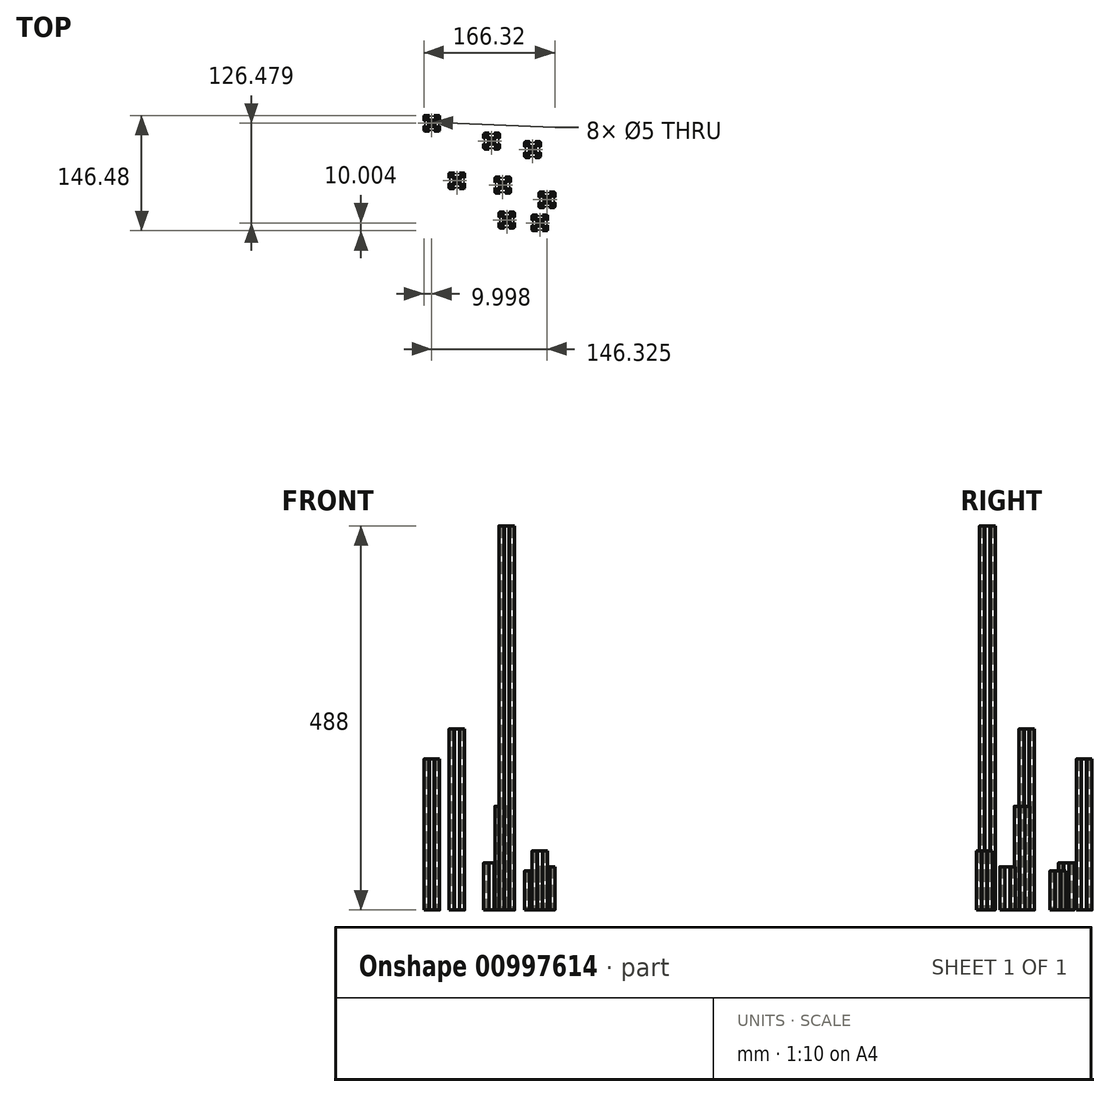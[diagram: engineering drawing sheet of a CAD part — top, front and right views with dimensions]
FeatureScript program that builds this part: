
annotation { "Feature Type Name" : "Feature", "Feature Type Description" : "" }
export const myFeature = defineFeature(function(context is Context, id is Id, definition is map)
    precondition{}
    {
        {
            var Q0;
            Q0=qCreatedBy(makeId("Top.planeOp"),FACE);
            var sketch = newSketch(context, id + "F0", { "sketchPlane" : qUnion([Q0])});
            skCircle(sketch, "E0", {"center": v(-239.3, 88.48) * mm, "radius": 2.5 * mm});
            skLineSegment(sketch, "E1.bottom", {"start": v(-230.8, 78.48) * mm, "end": v(-235.2, 78.48) * mm});
            skLineSegment(sketch, "E1.top", {"start": v(-230.8, 98.48) * mm, "end": v(-235.2, 98.48) * mm});
            skLineSegment(sketch, "E1.left", {"start": v(-229.3, 79.98) * mm, "end": v(-229.3, 84.88) * mm});
            skLineSegment(sketch, "E2.bottom", {"start": v(-237.3, 84.58) * mm, "end": v(-241.31, 84.58) * mm});
            skLineSegment(sketch, "E2.top", {"start": v(-237.3, 92.38) * mm, "end": v(-241.31, 92.38) * mm});
            skLineSegment(sketch, "E2.left", {"start": v(-235.4, 86.47) * mm, "end": v(-235.4, 90.5) * mm});
            skLineSegment(sketch, "E2.right", {"start": v(-243.2, 86.47) * mm, "end": v(-243.2, 90.5) * mm});
            skLineSegment(sketch, "E3.bottom", {"start": v(-230.8, 98.48) * mm, "end": v(-233.8, 98.48) * mm});
            skLineSegment(sketch, "E3.left", {"start": v(-229.3, 96.98) * mm, "end": v(-229.3, 93.98) * mm});
            skLineSegment(sketch, "E3.right", {"start": v(-233.8, 96.68) * mm, "end": v(-233.8, 95.04) * mm});
            skLineSegment(sketch, "E4", {"start": v(-234.82, 91.9) * mm, "end": v(-232.74, 93.98) * mm});
            skLineSegment(sketch, "E5.MirrorCS", {"start": v(-235.88, 92.97) * mm, "end": v(-233.8, 95.04) * mm});
            skLineSegment(sketch, "E6", {"start": v(-231.1, 93.98) * mm, "end": v(-231.1, 91.58) * mm});
            skLineSegment(sketch, "E7", {"start": v(-229.6, 92.08) * mm, "end": v(-229.3, 92.08) * mm});
            skLineSegment(sketch, "E8", {"start": v(-231.1, 91.58) * mm, "end": v(-229.8, 91.58) * mm});
            skLineSegment(sketch, "E9", {"start": v(-229.8, 91.88) * mm, "end": v(-229.8, 91.58) * mm});
            skPoint(sketch, "E10.visualSharp", {"position": v(-229.8, 92.08) * mm});
            skArc(sketch, "E10.filletArc", {"start": v(-229.6, 92.08) * mm, "mid": v(-229.74, 92.03) * mm, "end": v(-229.8, 91.88) * mm});
            skPoint(sketch, "E11.newPointA", {"position": v(-235.4, 91.32) * mm});
            skArc(sketch, "E11.filletArc", {"start": v(-234.82, 91.9) * mm, "mid": v(-235.25, 91.26) * mm, "end": v(-235.4, 90.5) * mm});
            skPoint(sketch, "E12.newPointA", {"position": v(-236.46, 92.38) * mm});
            skPoint(sketch, "E12.newPointB", {"position": v(-235.4, 92.38) * mm});
            skArc(sketch, "E12.filletArc", {"start": v(-237.3, 92.38) * mm, "mid": v(-236.53, 92.54) * mm, "end": v(-235.88, 92.97) * mm});
            skLineSegment(sketch, "E13.MirrorCS", {"start": v(-233.8, 96.68) * mm, "end": v(-236.2, 96.68) * mm});
            skLineSegment(sketch, "E14.MirrorCS", {"start": v(-236.2, 96.68) * mm, "end": v(-236.2, 97.98) * mm});
            skPoint(sketch, "E15.visualSharp", {"position": v(-229.3, 98.48) * mm});
            skArc(sketch, "E15.filletArc", {"start": v(-229.3, 96.98) * mm, "mid": v(-229.74, 98.04) * mm, "end": v(-230.8, 98.48) * mm});
            skLineSegment(sketch, "E16.trimOffspring", {"start": v(-231.1, 93.98) * mm, "end": v(-232.74, 93.98) * mm});
            skLineSegment(sketch, "E17.MirrorCS", {"start": v(-229.6, 84.88) * mm, "end": v(-229.3, 84.88) * mm});
            skArc(sketch, "E18.MirrorCS", {"start": v(-229.6, 84.88) * mm, "mid": v(-229.74, 84.94) * mm, "end": v(-229.8, 85.08) * mm});
            skLineSegment(sketch, "E19.MirrorCS", {"start": v(-229.8, 85.08) * mm, "end": v(-229.8, 85.38) * mm});
            skArc(sketch, "E20.MirrorCS", {"start": v(-234.82, 85.06) * mm, "mid": v(-235.25, 85.7) * mm, "end": v(-235.4, 86.47) * mm});
            skLineSegment(sketch, "E21.MirrorCS", {"start": v(-231.1, 82.98) * mm, "end": v(-232.74, 82.98) * mm});
            skLineSegment(sketch, "E22.MirrorCS", {"start": v(-231.1, 85.38) * mm, "end": v(-229.8, 85.38) * mm});
            skLineSegment(sketch, "E23.MirrorCS", {"start": v(-230.8, 78.48) * mm, "end": v(-233.8, 78.48) * mm});
            skPoint(sketch, "E24.MirrorP", {"position": v(-229.8, 84.88) * mm});
            skLineSegment(sketch, "E25.MirrorCS", {"start": v(-236.2, 80.28) * mm, "end": v(-236.2, 78.98) * mm});
            skLineSegment(sketch, "E26.MirrorCS", {"start": v(-233.8, 80.28) * mm, "end": v(-236.2, 80.28) * mm});
            skLineSegment(sketch, "E27.MirrorCS", {"start": v(-231.1, 82.98) * mm, "end": v(-231.1, 85.38) * mm});
            skLineSegment(sketch, "E28.MirrorCS", {"start": v(-229.3, 79.98) * mm, "end": v(-229.3, 82.98) * mm});
            skLineSegment(sketch, "E29.MirrorCS", {"start": v(-234.82, 85.06) * mm, "end": v(-232.74, 82.98) * mm});
            skPoint(sketch, "E30.MirrorP", {"position": v(-235.4, 85.64) * mm});
            skPoint(sketch, "E31.MirrorP", {"position": v(-229.3, 78.48) * mm});
            skPoint(sketch, "E32.MirrorP", {"position": v(-235.4, 84.58) * mm});
            skLineSegment(sketch, "E33.MirrorCS", {"start": v(-235.88, 84) * mm, "end": v(-233.8, 81.92) * mm});
            skPoint(sketch, "E34.MirrorP", {"position": v(-236.46, 84.58) * mm});
            skArc(sketch, "E35.MirrorCS", {"start": v(-229.3, 79.98) * mm, "mid": v(-229.74, 78.92) * mm, "end": v(-230.8, 78.48) * mm});
            skLineSegment(sketch, "E36.MirrorCS", {"start": v(-233.8, 80.28) * mm, "end": v(-233.8, 81.92) * mm});
            skArc(sketch, "E37.MirrorCS", {"start": v(-237.3, 84.58) * mm, "mid": v(-236.53, 84.43) * mm, "end": v(-235.88, 84) * mm});
            skLineSegment(sketch, "E38.trimOffspring", {"start": v(-229.3, 92.08) * mm, "end": v(-229.3, 96.98) * mm});
            skLineSegment(sketch, "E39.MirrorCS", {"start": v(-235.7, 98.18) * mm, "end": v(-235.7, 98.48) * mm});
            skArc(sketch, "E40.MirrorCS", {"start": v(-235.7, 98.18) * mm, "mid": v(-235.76, 98.04) * mm, "end": v(-235.9, 97.98) * mm});
            skLineSegment(sketch, "E41.MirrorCS", {"start": v(-235.9, 97.98) * mm, "end": v(-236.2, 97.98) * mm});
            skLineSegment(sketch, "E42", {"start": v(-235.2, 98.48) * mm, "end": v(-235.7, 98.48) * mm});
            skLineSegment(sketch, "E43.MirrorCS", {"start": v(-235.7, 78.78) * mm, "end": v(-235.7, 78.48) * mm});
            skLineSegment(sketch, "E44.MirrorCS", {"start": v(-235.9, 78.98) * mm, "end": v(-236.2, 78.98) * mm});
            skLineSegment(sketch, "E45.MirrorCS", {"start": v(-235.2, 78.48) * mm, "end": v(-235.7, 78.48) * mm});
            skArc(sketch, "E46.MirrorCS", {"start": v(-235.7, 78.78) * mm, "mid": v(-235.76, 78.93) * mm, "end": v(-235.9, 78.98) * mm});
            skArc(sketch, "E47.MirrorCS", {"start": v(-249, 84.88) * mm, "mid": v(-248.86, 84.94) * mm, "end": v(-248.8, 85.08) * mm});
            skLineSegment(sketch, "E48.MirrorCS", {"start": v(-249, 92.08) * mm, "end": v(-249.3, 92.08) * mm});
            skLineSegment(sketch, "E49.MirrorCS", {"start": v(-248.8, 85.08) * mm, "end": v(-248.8, 85.38) * mm});
            skArc(sketch, "E50.MirrorCS", {"start": v(-249, 92.08) * mm, "mid": v(-248.86, 92.03) * mm, "end": v(-248.8, 91.88) * mm});
            skLineSegment(sketch, "E51.MirrorCS", {"start": v(-248.8, 91.88) * mm, "end": v(-248.8, 91.58) * mm});
            skLineSegment(sketch, "E52.MirrorCS", {"start": v(-249, 84.88) * mm, "end": v(-249.3, 84.88) * mm});
            skLineSegment(sketch, "E53.MirrorCS", {"start": v(-243.4, 98.48) * mm, "end": v(-242.9, 98.48) * mm});
            skArc(sketch, "E54.MirrorCS", {"start": v(-249.3, 79.98) * mm, "mid": v(-248.86, 78.92) * mm, "end": v(-247.8, 78.48) * mm});
            skLineSegment(sketch, "E55.MirrorCS", {"start": v(-242.9, 98.18) * mm, "end": v(-242.9, 98.48) * mm});
            skArc(sketch, "E56.MirrorCS", {"start": v(-243.79, 91.9) * mm, "mid": v(-243.35, 91.26) * mm, "end": v(-243.2, 90.5) * mm});
            skLineSegment(sketch, "E57.MirrorCS", {"start": v(-242.7, 78.98) * mm, "end": v(-242.4, 78.98) * mm});
            skLineSegment(sketch, "E58.MirrorCS", {"start": v(-242.4, 96.68) * mm, "end": v(-242.4, 97.98) * mm});
            skLineSegment(sketch, "E59.MirrorCS", {"start": v(-241.31, 92.38) * mm, "end": v(-237.3, 92.38) * mm});
            skLineSegment(sketch, "E60.MirrorCS", {"start": v(-247.5, 85.38) * mm, "end": v(-248.8, 85.38) * mm});
            skLineSegment(sketch, "E61.MirrorCS", {"start": v(-247.5, 91.58) * mm, "end": v(-248.8, 91.58) * mm});
            skLineSegment(sketch, "E62.MirrorCS", {"start": v(-242.7, 97.98) * mm, "end": v(-242.4, 97.98) * mm});
            skArc(sketch, "E63.MirrorCS", {"start": v(-243.79, 85.06) * mm, "mid": v(-243.35, 85.7) * mm, "end": v(-243.2, 86.47) * mm});
            skArc(sketch, "E64.MirrorCS", {"start": v(-242.9, 78.78) * mm, "mid": v(-242.84, 78.93) * mm, "end": v(-242.7, 78.98) * mm});
            skArc(sketch, "E65.MirrorCS", {"start": v(-242.9, 98.18) * mm, "mid": v(-242.84, 98.04) * mm, "end": v(-242.7, 97.98) * mm});
            skLineSegment(sketch, "E66.MirrorCS", {"start": v(-242.9, 78.78) * mm, "end": v(-242.9, 78.48) * mm});
            skLineSegment(sketch, "E67.MirrorCS", {"start": v(-241.31, 84.58) * mm, "end": v(-237.3, 84.58) * mm});
            skLineSegment(sketch, "E68.MirrorCS", {"start": v(-243.4, 78.48) * mm, "end": v(-242.9, 78.48) * mm});
            skLineSegment(sketch, "E69.MirrorCS", {"start": v(-242.4, 80.28) * mm, "end": v(-242.4, 78.98) * mm});
            skArc(sketch, "E70.MirrorCS", {"start": v(-241.31, 92.38) * mm, "mid": v(-242.08, 92.54) * mm, "end": v(-242.73, 92.97) * mm});
            skPoint(sketch, "E71.MirrorP", {"position": v(-249.3, 78.48) * mm});
            skLineSegment(sketch, "E72.MirrorCS", {"start": v(-247.8, 78.48) * mm, "end": v(-243.4, 78.48) * mm});
            skPoint(sketch, "E73.MirrorP", {"position": v(-243.2, 84.58) * mm});
            skLineSegment(sketch, "E74.MirrorCS", {"start": v(-247.8, 98.48) * mm, "end": v(-243.4, 98.48) * mm});
            skArc(sketch, "E75.MirrorCS", {"start": v(-241.31, 84.58) * mm, "mid": v(-242.08, 84.43) * mm, "end": v(-242.73, 84) * mm});
            skArc(sketch, "E76.MirrorCS", {"start": v(-249.3, 96.98) * mm, "mid": v(-248.86, 98.04) * mm, "end": v(-247.8, 98.48) * mm});
            skPoint(sketch, "E77.MirrorP", {"position": v(-243.2, 85.64) * mm});
            skLineSegment(sketch, "E78.MirrorCS", {"start": v(-244.8, 96.68) * mm, "end": v(-244.8, 95.04) * mm});
            skLineSegment(sketch, "E79.MirrorCS", {"start": v(-242.73, 92.97) * mm, "end": v(-244.8, 95.04) * mm});
            skPoint(sketch, "E80.MirrorP", {"position": v(-243.2, 91.32) * mm});
            skLineSegment(sketch, "E81.MirrorCS", {"start": v(-247.5, 82.98) * mm, "end": v(-247.5, 85.38) * mm});
            skLineSegment(sketch, "E82.MirrorCS", {"start": v(-243.79, 85.06) * mm, "end": v(-245.86, 82.98) * mm});
            skLineSegment(sketch, "E83.MirrorCS", {"start": v(-244.8, 80.28) * mm, "end": v(-242.4, 80.28) * mm});
            skLineSegment(sketch, "E84.MirrorCS", {"start": v(-247.5, 82.98) * mm, "end": v(-245.86, 82.98) * mm});
            skLineSegment(sketch, "E85.MirrorCS", {"start": v(-249.3, 79.98) * mm, "end": v(-249.3, 82.98) * mm});
            skLineSegment(sketch, "E86.MirrorCS", {"start": v(-247.8, 98.48) * mm, "end": v(-244.8, 98.48) * mm});
            skLineSegment(sketch, "E87.MirrorCS", {"start": v(-249.3, 92.08) * mm, "end": v(-249.3, 96.98) * mm});
            skLineSegment(sketch, "E88.MirrorCS", {"start": v(-244.8, 96.68) * mm, "end": v(-242.4, 96.68) * mm});
            skLineSegment(sketch, "E89.MirrorCS", {"start": v(-242.73, 84) * mm, "end": v(-244.8, 81.92) * mm});
            skPoint(sketch, "E90.MirrorP", {"position": v(-242.14, 84.58) * mm});
            skLineSegment(sketch, "E91.MirrorCS", {"start": v(-247.5, 93.98) * mm, "end": v(-247.5, 91.58) * mm});
            skLineSegment(sketch, "E92.MirrorCS", {"start": v(-249.3, 96.98) * mm, "end": v(-249.3, 93.98) * mm});
            skPoint(sketch, "E93.MirrorP", {"position": v(-248.8, 84.88) * mm});
            skPoint(sketch, "E94.MirrorP", {"position": v(-249.3, 98.48) * mm});
            skPoint(sketch, "E95.MirrorP", {"position": v(-248.8, 92.08) * mm});
            skLineSegment(sketch, "E96.MirrorCS", {"start": v(-243.79, 91.9) * mm, "end": v(-245.86, 93.98) * mm});
            skLineSegment(sketch, "E97.MirrorCS", {"start": v(-247.5, 93.98) * mm, "end": v(-245.86, 93.98) * mm});
            skLineSegment(sketch, "E98.MirrorCS", {"start": v(-249.3, 79.98) * mm, "end": v(-249.3, 84.88) * mm});
            skLineSegment(sketch, "E99.MirrorCS", {"start": v(-247.8, 78.48) * mm, "end": v(-244.8, 78.48) * mm});
            skPoint(sketch, "E100.MirrorP", {"position": v(-243.2, 92.38) * mm});
            skPoint(sketch, "E101.MirrorP", {"position": v(-242.14, 92.38) * mm});
            skLineSegment(sketch, "E102.MirrorCS", {"start": v(-244.8, 80.28) * mm, "end": v(-244.8, 81.92) * mm});
            skSolve(sketch);
        }
        {
            var Q0;
            Q0=makeQuery(id+"F0.imprint","IMPRINT",FACE,{"disambiguationData":[TD([[makeQuery(id+"F0.imprint","IMPRINT",EDGE,{"derivedFrom":sQuery(id+"F0.wireOp",EDGE,"E1.bottom")}),-1.0]])]});
            extrude(context, id + "F1", {"entities" : qUnion([Q0]), "depth" : 192 * mm, "offsetDistance" : 25 * mm});
        }
        {
            var Q0;
            Q0=qCreatedBy(makeId("Top.planeOp"),FACE);
            var sketch = newSketch(context, id + "F2", { "sketchPlane" : qUnion([Q0])});
            skCircle(sketch, "E103", {"center": v(-207.4, 15.55) * mm, "radius": 2.5 * mm});
            skLineSegment(sketch, "E104.bottom", {"start": v(-198.9, 5.55) * mm, "end": v(-203.3, 5.55) * mm});
            skLineSegment(sketch, "E104.top", {"start": v(-198.9, 25.55) * mm, "end": v(-203.3, 25.55) * mm});
            skLineSegment(sketch, "E104.left", {"start": v(-197.4, 7.05) * mm, "end": v(-197.4, 11.95) * mm});
            skLineSegment(sketch, "E105.bottom", {"start": v(-205.4, 11.65) * mm, "end": v(-209.42, 11.65) * mm});
            skLineSegment(sketch, "E105.top", {"start": v(-205.4, 19.45) * mm, "end": v(-209.42, 19.45) * mm});
            skLineSegment(sketch, "E105.left", {"start": v(-203.5, 13.54) * mm, "end": v(-203.5, 17.56) * mm});
            skLineSegment(sketch, "E105.right", {"start": v(-211.3, 13.54) * mm, "end": v(-211.3, 17.56) * mm});
            skLineSegment(sketch, "E106.bottom", {"start": v(-198.9, 25.55) * mm, "end": v(-201.9, 25.55) * mm});
            skLineSegment(sketch, "E106.left", {"start": v(-197.4, 24.05) * mm, "end": v(-197.4, 21.05) * mm});
            skLineSegment(sketch, "E106.right", {"start": v(-201.9, 23.75) * mm, "end": v(-201.9, 22.1) * mm});
            skLineSegment(sketch, "E107", {"start": v(-202.92, 18.97) * mm, "end": v(-200.84, 21.05) * mm});
            skLineSegment(sketch, "E108.MirrorCS", {"start": v(-203.98, 20.04) * mm, "end": v(-201.9, 22.1) * mm});
            skLineSegment(sketch, "E109", {"start": v(-199.2, 21.05) * mm, "end": v(-199.2, 18.65) * mm});
            skLineSegment(sketch, "E110", {"start": v(-197.7, 19.15) * mm, "end": v(-197.4, 19.15) * mm});
            skLineSegment(sketch, "E111", {"start": v(-199.2, 18.65) * mm, "end": v(-197.9, 18.65) * mm});
            skLineSegment(sketch, "E112", {"start": v(-197.9, 18.95) * mm, "end": v(-197.9, 18.65) * mm});
            skPoint(sketch, "E113.visualSharp", {"position": v(-197.9, 19.15) * mm});
            skArc(sketch, "E113.filletArc", {"start": v(-197.7, 19.15) * mm, "mid": v(-197.85, 19.1) * mm, "end": v(-197.9, 18.95) * mm});
            skPoint(sketch, "E114.newPointA", {"position": v(-203.5, 18.39) * mm});
            skArc(sketch, "E114.filletArc", {"start": v(-202.92, 18.97) * mm, "mid": v(-203.35, 18.33) * mm, "end": v(-203.5, 17.56) * mm});
            skPoint(sketch, "E115.newPointA", {"position": v(-204.57, 19.45) * mm});
            skPoint(sketch, "E115.newPointB", {"position": v(-203.5, 19.45) * mm});
            skArc(sketch, "E115.filletArc", {"start": v(-205.4, 19.45) * mm, "mid": v(-204.63, 19.6) * mm, "end": v(-203.98, 20.04) * mm});
            skLineSegment(sketch, "E116.MirrorCS", {"start": v(-201.9, 23.75) * mm, "end": v(-204.3, 23.75) * mm});
            skLineSegment(sketch, "E117.MirrorCS", {"start": v(-204.3, 23.75) * mm, "end": v(-204.3, 25.05) * mm});
            skPoint(sketch, "E118.visualSharp", {"position": v(-197.4, 25.55) * mm});
            skArc(sketch, "E118.filletArc", {"start": v(-197.4, 24.05) * mm, "mid": v(-197.84, 25.1) * mm, "end": v(-198.9, 25.55) * mm});
            skLineSegment(sketch, "E119.trimOffspring", {"start": v(-199.2, 21.05) * mm, "end": v(-200.84, 21.05) * mm});
            skLineSegment(sketch, "E120.MirrorCS", {"start": v(-197.7, 11.95) * mm, "end": v(-197.4, 11.95) * mm});
            skArc(sketch, "E121.MirrorCS", {"start": v(-197.7, 11.95) * mm, "mid": v(-197.85, 12) * mm, "end": v(-197.9, 12.15) * mm});
            skLineSegment(sketch, "E122.MirrorCS", {"start": v(-197.9, 12.15) * mm, "end": v(-197.9, 12.45) * mm});
            skArc(sketch, "E123.MirrorCS", {"start": v(-202.92, 12.12) * mm, "mid": v(-203.35, 12.77) * mm, "end": v(-203.5, 13.54) * mm});
            skLineSegment(sketch, "E124.MirrorCS", {"start": v(-199.2, 10.05) * mm, "end": v(-200.84, 10.05) * mm});
            skLineSegment(sketch, "E125.MirrorCS", {"start": v(-199.2, 12.45) * mm, "end": v(-197.9, 12.45) * mm});
            skLineSegment(sketch, "E126.MirrorCS", {"start": v(-198.9, 5.55) * mm, "end": v(-201.9, 5.55) * mm});
            skPoint(sketch, "E127.MirrorP", {"position": v(-197.9, 11.95) * mm});
            skLineSegment(sketch, "E128.MirrorCS", {"start": v(-204.3, 7.35) * mm, "end": v(-204.3, 6.05) * mm});
            skLineSegment(sketch, "E129.MirrorCS", {"start": v(-201.9, 7.35) * mm, "end": v(-204.3, 7.35) * mm});
            skLineSegment(sketch, "E130.MirrorCS", {"start": v(-199.2, 10.05) * mm, "end": v(-199.2, 12.45) * mm});
            skLineSegment(sketch, "E131.MirrorCS", {"start": v(-197.4, 7.05) * mm, "end": v(-197.4, 10.05) * mm});
            skLineSegment(sketch, "E132.MirrorCS", {"start": v(-202.92, 12.12) * mm, "end": v(-200.84, 10.05) * mm});
            skPoint(sketch, "E133.MirrorP", {"position": v(-203.5, 12.7) * mm});
            skPoint(sketch, "E134.MirrorP", {"position": v(-197.4, 5.55) * mm});
            skPoint(sketch, "E135.MirrorP", {"position": v(-203.5, 11.65) * mm});
            skLineSegment(sketch, "E136.MirrorCS", {"start": v(-203.98, 11.06) * mm, "end": v(-201.9, 8.99) * mm});
            skPoint(sketch, "E137.MirrorP", {"position": v(-204.57, 11.65) * mm});
            skArc(sketch, "E138.MirrorCS", {"start": v(-197.4, 7.05) * mm, "mid": v(-197.84, 5.99) * mm, "end": v(-198.9, 5.55) * mm});
            skLineSegment(sketch, "E139.MirrorCS", {"start": v(-201.9, 7.35) * mm, "end": v(-201.9, 8.99) * mm});
            skArc(sketch, "E140.MirrorCS", {"start": v(-205.4, 11.65) * mm, "mid": v(-204.63, 11.5) * mm, "end": v(-203.98, 11.06) * mm});
            skLineSegment(sketch, "E141.trimOffspring", {"start": v(-197.4, 19.15) * mm, "end": v(-197.4, 24.05) * mm});
            skLineSegment(sketch, "E142.MirrorCS", {"start": v(-203.8, 25.25) * mm, "end": v(-203.8, 25.55) * mm});
            skArc(sketch, "E143.MirrorCS", {"start": v(-203.8, 25.25) * mm, "mid": v(-203.86, 25.1) * mm, "end": v(-204, 25.05) * mm});
            skLineSegment(sketch, "E144.MirrorCS", {"start": v(-204, 25.05) * mm, "end": v(-204.3, 25.05) * mm});
            skLineSegment(sketch, "E145", {"start": v(-203.3, 25.55) * mm, "end": v(-203.8, 25.55) * mm});
            skLineSegment(sketch, "E146.MirrorCS", {"start": v(-203.8, 5.85) * mm, "end": v(-203.8, 5.55) * mm});
            skLineSegment(sketch, "E147.MirrorCS", {"start": v(-204, 6.05) * mm, "end": v(-204.3, 6.05) * mm});
            skLineSegment(sketch, "E148.MirrorCS", {"start": v(-203.3, 5.55) * mm, "end": v(-203.8, 5.55) * mm});
            skArc(sketch, "E149.MirrorCS", {"start": v(-203.8, 5.85) * mm, "mid": v(-203.86, 6) * mm, "end": v(-204, 6.05) * mm});
            skArc(sketch, "E150.MirrorCS", {"start": v(-217.1, 11.95) * mm, "mid": v(-216.96, 12) * mm, "end": v(-216.9, 12.15) * mm});
            skLineSegment(sketch, "E151.MirrorCS", {"start": v(-217.1, 19.15) * mm, "end": v(-217.4, 19.15) * mm});
            skLineSegment(sketch, "E152.MirrorCS", {"start": v(-216.9, 12.15) * mm, "end": v(-216.9, 12.45) * mm});
            skArc(sketch, "E153.MirrorCS", {"start": v(-217.1, 19.15) * mm, "mid": v(-216.96, 19.1) * mm, "end": v(-216.9, 18.95) * mm});
            skLineSegment(sketch, "E154.MirrorCS", {"start": v(-216.9, 18.95) * mm, "end": v(-216.9, 18.65) * mm});
            skLineSegment(sketch, "E155.MirrorCS", {"start": v(-217.1, 11.95) * mm, "end": v(-217.4, 11.95) * mm});
            skLineSegment(sketch, "E156.MirrorCS", {"start": v(-211.5, 25.55) * mm, "end": v(-211, 25.55) * mm});
            skArc(sketch, "E157.MirrorCS", {"start": v(-217.4, 7.05) * mm, "mid": v(-216.97, 5.99) * mm, "end": v(-215.9, 5.55) * mm});
            skLineSegment(sketch, "E158.MirrorCS", {"start": v(-211, 25.25) * mm, "end": v(-211, 25.55) * mm});
            skArc(sketch, "E159.MirrorCS", {"start": v(-211.9, 18.97) * mm, "mid": v(-211.46, 18.33) * mm, "end": v(-211.3, 17.56) * mm});
            skLineSegment(sketch, "E160.MirrorCS", {"start": v(-210.8, 6.05) * mm, "end": v(-210.5, 6.05) * mm});
            skLineSegment(sketch, "E161.MirrorCS", {"start": v(-210.5, 23.75) * mm, "end": v(-210.5, 25.05) * mm});
            skLineSegment(sketch, "E162.MirrorCS", {"start": v(-209.42, 19.45) * mm, "end": v(-205.4, 19.45) * mm});
            skLineSegment(sketch, "E163.MirrorCS", {"start": v(-215.6, 12.45) * mm, "end": v(-216.9, 12.45) * mm});
            skLineSegment(sketch, "E164.MirrorCS", {"start": v(-215.6, 18.65) * mm, "end": v(-216.9, 18.65) * mm});
            skLineSegment(sketch, "E165.MirrorCS", {"start": v(-210.8, 25.05) * mm, "end": v(-210.5, 25.05) * mm});
            skArc(sketch, "E166.MirrorCS", {"start": v(-211.9, 12.12) * mm, "mid": v(-211.46, 12.77) * mm, "end": v(-211.3, 13.54) * mm});
            skArc(sketch, "E167.MirrorCS", {"start": v(-211, 5.85) * mm, "mid": v(-210.95, 6) * mm, "end": v(-210.8, 6.05) * mm});
            skArc(sketch, "E168.MirrorCS", {"start": v(-211, 25.25) * mm, "mid": v(-210.95, 25.1) * mm, "end": v(-210.8, 25.05) * mm});
            skLineSegment(sketch, "E169.MirrorCS", {"start": v(-211, 5.85) * mm, "end": v(-211, 5.55) * mm});
            skLineSegment(sketch, "E170.MirrorCS", {"start": v(-209.42, 11.65) * mm, "end": v(-205.4, 11.65) * mm});
            skLineSegment(sketch, "E171.MirrorCS", {"start": v(-211.5, 5.55) * mm, "end": v(-211, 5.55) * mm});
            skLineSegment(sketch, "E172.MirrorCS", {"start": v(-210.5, 7.35) * mm, "end": v(-210.5, 6.05) * mm});
            skArc(sketch, "E173.MirrorCS", {"start": v(-209.42, 19.45) * mm, "mid": v(-210.18, 19.6) * mm, "end": v(-210.83, 20.04) * mm});
            skPoint(sketch, "E174.MirrorP", {"position": v(-217.4, 5.55) * mm});
            skLineSegment(sketch, "E175.MirrorCS", {"start": v(-215.9, 5.55) * mm, "end": v(-211.5, 5.55) * mm});
            skPoint(sketch, "E176.MirrorP", {"position": v(-211.3, 11.65) * mm});
            skLineSegment(sketch, "E177.MirrorCS", {"start": v(-215.9, 25.55) * mm, "end": v(-211.5, 25.55) * mm});
            skArc(sketch, "E178.MirrorCS", {"start": v(-209.42, 11.65) * mm, "mid": v(-210.18, 11.5) * mm, "end": v(-210.83, 11.06) * mm});
            skArc(sketch, "E179.MirrorCS", {"start": v(-217.4, 24.05) * mm, "mid": v(-216.97, 25.1) * mm, "end": v(-215.9, 25.55) * mm});
            skPoint(sketch, "E180.MirrorP", {"position": v(-211.3, 12.7) * mm});
            skLineSegment(sketch, "E181.MirrorCS", {"start": v(-212.9, 23.75) * mm, "end": v(-212.9, 22.1) * mm});
            skLineSegment(sketch, "E182.MirrorCS", {"start": v(-210.83, 20.04) * mm, "end": v(-212.9, 22.1) * mm});
            skPoint(sketch, "E183.MirrorP", {"position": v(-211.3, 18.39) * mm});
            skLineSegment(sketch, "E184.MirrorCS", {"start": v(-215.6, 10.05) * mm, "end": v(-215.6, 12.45) * mm});
            skLineSegment(sketch, "E185.MirrorCS", {"start": v(-211.9, 12.12) * mm, "end": v(-213.97, 10.05) * mm});
            skLineSegment(sketch, "E186.MirrorCS", {"start": v(-212.9, 7.35) * mm, "end": v(-210.5, 7.35) * mm});
            skLineSegment(sketch, "E187.MirrorCS", {"start": v(-215.6, 10.05) * mm, "end": v(-213.97, 10.05) * mm});
            skLineSegment(sketch, "E188.MirrorCS", {"start": v(-217.4, 7.05) * mm, "end": v(-217.4, 10.05) * mm});
            skLineSegment(sketch, "E189.MirrorCS", {"start": v(-215.9, 25.55) * mm, "end": v(-212.9, 25.55) * mm});
            skLineSegment(sketch, "E190.MirrorCS", {"start": v(-217.4, 19.15) * mm, "end": v(-217.4, 24.05) * mm});
            skLineSegment(sketch, "E191.MirrorCS", {"start": v(-212.9, 23.75) * mm, "end": v(-210.5, 23.75) * mm});
            skLineSegment(sketch, "E192.MirrorCS", {"start": v(-210.83, 11.06) * mm, "end": v(-212.9, 8.99) * mm});
            skPoint(sketch, "E193.MirrorP", {"position": v(-210.24, 11.65) * mm});
            skLineSegment(sketch, "E194.MirrorCS", {"start": v(-215.6, 21.05) * mm, "end": v(-215.6, 18.65) * mm});
            skLineSegment(sketch, "E195.MirrorCS", {"start": v(-217.4, 24.05) * mm, "end": v(-217.4, 21.05) * mm});
            skPoint(sketch, "E196.MirrorP", {"position": v(-216.9, 11.95) * mm});
            skPoint(sketch, "E197.MirrorP", {"position": v(-217.4, 25.55) * mm});
            skPoint(sketch, "E198.MirrorP", {"position": v(-216.9, 19.15) * mm});
            skLineSegment(sketch, "E199.MirrorCS", {"start": v(-211.9, 18.97) * mm, "end": v(-213.97, 21.05) * mm});
            skLineSegment(sketch, "E200.MirrorCS", {"start": v(-215.6, 21.05) * mm, "end": v(-213.97, 21.05) * mm});
            skLineSegment(sketch, "E201.MirrorCS", {"start": v(-217.4, 7.05) * mm, "end": v(-217.4, 11.95) * mm});
            skLineSegment(sketch, "E202.MirrorCS", {"start": v(-215.9, 5.55) * mm, "end": v(-212.9, 5.55) * mm});
            skPoint(sketch, "E203.MirrorP", {"position": v(-211.3, 19.45) * mm});
            skPoint(sketch, "E204.MirrorP", {"position": v(-210.24, 19.45) * mm});
            skLineSegment(sketch, "E205.MirrorCS", {"start": v(-212.9, 7.35) * mm, "end": v(-212.9, 8.99) * mm});
            skSolve(sketch);
        }
        {
            var Q0;
            Q0=makeQuery(id+"F2.imprint","IMPRINT",FACE,{"disambiguationData":[TD([[makeQuery(id+"F2.imprint","IMPRINT",EDGE,{"derivedFrom":sQuery(id+"F2.wireOp",EDGE,"E104.bottom")}),-1.0]])]});
            extrude(context, id + "F3", {"entities" : qUnion([Q0]), "depth" : 230 * mm, "offsetDistance" : 25 * mm});
        }
        {
            var Q0;
            Q0=qCreatedBy(makeId("Top.planeOp"),FACE);
            var sketch = newSketch(context, id + "F4", { "sketchPlane" : qUnion([Q0])});
            skCircle(sketch, "E206", {"center": v(-163.25, 65.95) * mm, "radius": 2.5 * mm});
            skLineSegment(sketch, "E207.bottom", {"start": v(-154.75, 55.95) * mm, "end": v(-159.15, 55.95) * mm});
            skLineSegment(sketch, "E207.top", {"start": v(-154.75, 75.95) * mm, "end": v(-159.15, 75.95) * mm});
            skLineSegment(sketch, "E207.left", {"start": v(-153.25, 57.45) * mm, "end": v(-153.25, 62.35) * mm});
            skLineSegment(sketch, "E208.bottom", {"start": v(-161.24, 62.05) * mm, "end": v(-165.26, 62.05) * mm});
            skLineSegment(sketch, "E208.top", {"start": v(-161.24, 69.85) * mm, "end": v(-165.26, 69.85) * mm});
            skLineSegment(sketch, "E208.left", {"start": v(-159.35, 63.94) * mm, "end": v(-159.35, 67.96) * mm});
            skLineSegment(sketch, "E208.right", {"start": v(-167.15, 63.94) * mm, "end": v(-167.15, 67.96) * mm});
            skLineSegment(sketch, "E209.bottom", {"start": v(-154.75, 75.95) * mm, "end": v(-157.75, 75.95) * mm});
            skLineSegment(sketch, "E209.left", {"start": v(-153.25, 74.45) * mm, "end": v(-153.25, 71.45) * mm});
            skLineSegment(sketch, "E209.right", {"start": v(-157.75, 74.15) * mm, "end": v(-157.75, 72.51) * mm});
            skLineSegment(sketch, "E210", {"start": v(-158.76, 69.38) * mm, "end": v(-156.69, 71.45) * mm});
            skLineSegment(sketch, "E211.MirrorCS", {"start": v(-159.82, 70.44) * mm, "end": v(-157.75, 72.51) * mm});
            skLineSegment(sketch, "E212", {"start": v(-155.05, 71.45) * mm, "end": v(-155.05, 69.05) * mm});
            skLineSegment(sketch, "E213", {"start": v(-153.55, 69.55) * mm, "end": v(-153.25, 69.55) * mm});
            skLineSegment(sketch, "E214", {"start": v(-155.05, 69.05) * mm, "end": v(-153.75, 69.05) * mm});
            skLineSegment(sketch, "E215", {"start": v(-153.75, 69.35) * mm, "end": v(-153.75, 69.05) * mm});
            skPoint(sketch, "E216.visualSharp", {"position": v(-153.75, 69.55) * mm});
            skArc(sketch, "E216.filletArc", {"start": v(-153.55, 69.55) * mm, "mid": v(-153.7, 69.5) * mm, "end": v(-153.75, 69.35) * mm});
            skPoint(sketch, "E217.newPointA", {"position": v(-159.35, 68.8) * mm});
            skArc(sketch, "E217.filletArc", {"start": v(-158.76, 69.38) * mm, "mid": v(-159.2, 68.73) * mm, "end": v(-159.35, 67.96) * mm});
            skPoint(sketch, "E218.newPointA", {"position": v(-160.41, 69.85) * mm});
            skPoint(sketch, "E218.newPointB", {"position": v(-159.35, 69.85) * mm});
            skArc(sketch, "E218.filletArc", {"start": v(-161.24, 69.85) * mm, "mid": v(-160.47, 70) * mm, "end": v(-159.82, 70.44) * mm});
            skLineSegment(sketch, "E219.MirrorCS", {"start": v(-157.75, 74.15) * mm, "end": v(-160.15, 74.15) * mm});
            skLineSegment(sketch, "E220.MirrorCS", {"start": v(-160.15, 74.15) * mm, "end": v(-160.15, 75.45) * mm});
            skPoint(sketch, "E221.visualSharp", {"position": v(-153.25, 75.95) * mm});
            skArc(sketch, "E221.filletArc", {"start": v(-153.25, 74.45) * mm, "mid": v(-153.69, 75.51) * mm, "end": v(-154.75, 75.95) * mm});
            skLineSegment(sketch, "E222.trimOffspring", {"start": v(-155.05, 71.45) * mm, "end": v(-156.69, 71.45) * mm});
            skLineSegment(sketch, "E223.MirrorCS", {"start": v(-153.55, 62.35) * mm, "end": v(-153.25, 62.35) * mm});
            skArc(sketch, "E224.MirrorCS", {"start": v(-153.55, 62.35) * mm, "mid": v(-153.7, 62.4) * mm, "end": v(-153.75, 62.55) * mm});
            skLineSegment(sketch, "E225.MirrorCS", {"start": v(-153.75, 62.55) * mm, "end": v(-153.75, 62.85) * mm});
            skArc(sketch, "E226.MirrorCS", {"start": v(-158.76, 62.53) * mm, "mid": v(-159.2, 63.17) * mm, "end": v(-159.35, 63.94) * mm});
            skLineSegment(sketch, "E227.MirrorCS", {"start": v(-155.05, 60.45) * mm, "end": v(-156.69, 60.45) * mm});
            skLineSegment(sketch, "E228.MirrorCS", {"start": v(-155.05, 62.85) * mm, "end": v(-153.75, 62.85) * mm});
            skLineSegment(sketch, "E229.MirrorCS", {"start": v(-154.75, 55.95) * mm, "end": v(-157.75, 55.95) * mm});
            skPoint(sketch, "E230.MirrorP", {"position": v(-153.75, 62.35) * mm});
            skLineSegment(sketch, "E231.MirrorCS", {"start": v(-160.15, 57.75) * mm, "end": v(-160.15, 56.45) * mm});
            skLineSegment(sketch, "E232.MirrorCS", {"start": v(-157.75, 57.75) * mm, "end": v(-160.15, 57.75) * mm});
            skLineSegment(sketch, "E233.MirrorCS", {"start": v(-155.05, 60.45) * mm, "end": v(-155.05, 62.85) * mm});
            skLineSegment(sketch, "E234.MirrorCS", {"start": v(-153.25, 57.45) * mm, "end": v(-153.25, 60.45) * mm});
            skLineSegment(sketch, "E235.MirrorCS", {"start": v(-158.76, 62.53) * mm, "end": v(-156.69, 60.45) * mm});
            skPoint(sketch, "E236.MirrorP", {"position": v(-159.35, 63.11) * mm});
            skPoint(sketch, "E237.MirrorP", {"position": v(-153.25, 55.95) * mm});
            skPoint(sketch, "E238.MirrorP", {"position": v(-159.35, 62.05) * mm});
            skLineSegment(sketch, "E239.MirrorCS", {"start": v(-159.82, 61.47) * mm, "end": v(-157.75, 59.4) * mm});
            skPoint(sketch, "E240.MirrorP", {"position": v(-160.41, 62.05) * mm});
            skArc(sketch, "E241.MirrorCS", {"start": v(-153.25, 57.45) * mm, "mid": v(-153.69, 56.4) * mm, "end": v(-154.75, 55.95) * mm});
            skLineSegment(sketch, "E242.MirrorCS", {"start": v(-157.75, 57.75) * mm, "end": v(-157.75, 59.4) * mm});
            skArc(sketch, "E243.MirrorCS", {"start": v(-161.24, 62.05) * mm, "mid": v(-160.47, 61.9) * mm, "end": v(-159.82, 61.47) * mm});
            skLineSegment(sketch, "E244.trimOffspring", {"start": v(-153.25, 69.55) * mm, "end": v(-153.25, 74.45) * mm});
            skLineSegment(sketch, "E245.MirrorCS", {"start": v(-159.65, 75.65) * mm, "end": v(-159.65, 75.95) * mm});
            skArc(sketch, "E246.MirrorCS", {"start": v(-159.65, 75.65) * mm, "mid": v(-159.7, 75.5) * mm, "end": v(-159.85, 75.45) * mm});
            skLineSegment(sketch, "E247.MirrorCS", {"start": v(-159.85, 75.45) * mm, "end": v(-160.15, 75.45) * mm});
            skLineSegment(sketch, "E248", {"start": v(-159.15, 75.95) * mm, "end": v(-159.65, 75.95) * mm});
            skLineSegment(sketch, "E249.MirrorCS", {"start": v(-159.65, 56.25) * mm, "end": v(-159.65, 55.95) * mm});
            skLineSegment(sketch, "E250.MirrorCS", {"start": v(-159.85, 56.45) * mm, "end": v(-160.15, 56.45) * mm});
            skLineSegment(sketch, "E251.MirrorCS", {"start": v(-159.15, 55.95) * mm, "end": v(-159.65, 55.95) * mm});
            skArc(sketch, "E252.MirrorCS", {"start": v(-159.65, 56.25) * mm, "mid": v(-159.7, 56.4) * mm, "end": v(-159.85, 56.45) * mm});
            skArc(sketch, "E253.MirrorCS", {"start": v(-172.95, 62.35) * mm, "mid": v(-172.8, 62.4) * mm, "end": v(-172.75, 62.55) * mm});
            skLineSegment(sketch, "E254.MirrorCS", {"start": v(-172.95, 69.55) * mm, "end": v(-173.25, 69.55) * mm});
            skLineSegment(sketch, "E255.MirrorCS", {"start": v(-172.75, 62.55) * mm, "end": v(-172.75, 62.85) * mm});
            skArc(sketch, "E256.MirrorCS", {"start": v(-172.95, 69.55) * mm, "mid": v(-172.8, 69.5) * mm, "end": v(-172.75, 69.35) * mm});
            skLineSegment(sketch, "E257.MirrorCS", {"start": v(-172.75, 69.35) * mm, "end": v(-172.75, 69.05) * mm});
            skLineSegment(sketch, "E258.MirrorCS", {"start": v(-172.95, 62.35) * mm, "end": v(-173.25, 62.35) * mm});
            skLineSegment(sketch, "E259.MirrorCS", {"start": v(-167.35, 75.95) * mm, "end": v(-166.85, 75.95) * mm});
            skArc(sketch, "E260.MirrorCS", {"start": v(-173.25, 57.45) * mm, "mid": v(-172.81, 56.4) * mm, "end": v(-171.75, 55.95) * mm});
            skLineSegment(sketch, "E261.MirrorCS", {"start": v(-166.85, 75.65) * mm, "end": v(-166.85, 75.95) * mm});
            skArc(sketch, "E262.MirrorCS", {"start": v(-167.74, 69.38) * mm, "mid": v(-167.3, 68.73) * mm, "end": v(-167.15, 67.96) * mm});
            skLineSegment(sketch, "E263.MirrorCS", {"start": v(-166.65, 56.45) * mm, "end": v(-166.35, 56.45) * mm});
            skLineSegment(sketch, "E264.MirrorCS", {"start": v(-166.35, 74.15) * mm, "end": v(-166.35, 75.45) * mm});
            skLineSegment(sketch, "E265.MirrorCS", {"start": v(-165.26, 69.85) * mm, "end": v(-161.24, 69.85) * mm});
            skLineSegment(sketch, "E266.MirrorCS", {"start": v(-171.45, 62.85) * mm, "end": v(-172.75, 62.85) * mm});
            skLineSegment(sketch, "E267.MirrorCS", {"start": v(-171.45, 69.05) * mm, "end": v(-172.75, 69.05) * mm});
            skLineSegment(sketch, "E268.MirrorCS", {"start": v(-166.65, 75.45) * mm, "end": v(-166.35, 75.45) * mm});
            skArc(sketch, "E269.MirrorCS", {"start": v(-167.74, 62.53) * mm, "mid": v(-167.3, 63.17) * mm, "end": v(-167.15, 63.94) * mm});
            skArc(sketch, "E270.MirrorCS", {"start": v(-166.85, 56.25) * mm, "mid": v(-166.8, 56.4) * mm, "end": v(-166.65, 56.45) * mm});
            skArc(sketch, "E271.MirrorCS", {"start": v(-166.85, 75.65) * mm, "mid": v(-166.8, 75.5) * mm, "end": v(-166.65, 75.45) * mm});
            skLineSegment(sketch, "E272.MirrorCS", {"start": v(-166.85, 56.25) * mm, "end": v(-166.85, 55.95) * mm});
            skLineSegment(sketch, "E273.MirrorCS", {"start": v(-165.26, 62.05) * mm, "end": v(-161.24, 62.05) * mm});
            skLineSegment(sketch, "E274.MirrorCS", {"start": v(-167.35, 55.95) * mm, "end": v(-166.85, 55.95) * mm});
            skLineSegment(sketch, "E275.MirrorCS", {"start": v(-166.35, 57.75) * mm, "end": v(-166.35, 56.45) * mm});
            skArc(sketch, "E276.MirrorCS", {"start": v(-165.26, 69.85) * mm, "mid": v(-166.03, 70) * mm, "end": v(-166.67, 70.44) * mm});
            skPoint(sketch, "E277.MirrorP", {"position": v(-173.25, 55.95) * mm});
            skLineSegment(sketch, "E278.MirrorCS", {"start": v(-171.75, 55.95) * mm, "end": v(-167.35, 55.95) * mm});
            skPoint(sketch, "E279.MirrorP", {"position": v(-167.15, 62.05) * mm});
            skLineSegment(sketch, "E280.MirrorCS", {"start": v(-171.75, 75.95) * mm, "end": v(-167.35, 75.95) * mm});
            skArc(sketch, "E281.MirrorCS", {"start": v(-165.26, 62.05) * mm, "mid": v(-166.03, 61.9) * mm, "end": v(-166.67, 61.47) * mm});
            skArc(sketch, "E282.MirrorCS", {"start": v(-173.25, 74.45) * mm, "mid": v(-172.81, 75.51) * mm, "end": v(-171.75, 75.95) * mm});
            skPoint(sketch, "E283.MirrorP", {"position": v(-167.15, 63.11) * mm});
            skLineSegment(sketch, "E284.MirrorCS", {"start": v(-168.75, 74.15) * mm, "end": v(-168.75, 72.51) * mm});
            skLineSegment(sketch, "E285.MirrorCS", {"start": v(-166.67, 70.44) * mm, "end": v(-168.75, 72.51) * mm});
            skPoint(sketch, "E286.MirrorP", {"position": v(-167.15, 68.8) * mm});
            skLineSegment(sketch, "E287.MirrorCS", {"start": v(-171.45, 60.45) * mm, "end": v(-171.45, 62.85) * mm});
            skLineSegment(sketch, "E288.MirrorCS", {"start": v(-167.74, 62.53) * mm, "end": v(-169.81, 60.45) * mm});
            skLineSegment(sketch, "E289.MirrorCS", {"start": v(-168.75, 57.75) * mm, "end": v(-166.35, 57.75) * mm});
            skLineSegment(sketch, "E290.MirrorCS", {"start": v(-171.45, 60.45) * mm, "end": v(-169.81, 60.45) * mm});
            skLineSegment(sketch, "E291.MirrorCS", {"start": v(-173.25, 57.45) * mm, "end": v(-173.25, 60.45) * mm});
            skLineSegment(sketch, "E292.MirrorCS", {"start": v(-171.75, 75.95) * mm, "end": v(-168.75, 75.95) * mm});
            skLineSegment(sketch, "E293.MirrorCS", {"start": v(-173.25, 69.55) * mm, "end": v(-173.25, 74.45) * mm});
            skLineSegment(sketch, "E294.MirrorCS", {"start": v(-168.75, 74.15) * mm, "end": v(-166.35, 74.15) * mm});
            skLineSegment(sketch, "E295.MirrorCS", {"start": v(-166.67, 61.47) * mm, "end": v(-168.75, 59.4) * mm});
            skPoint(sketch, "E296.MirrorP", {"position": v(-166.09, 62.05) * mm});
            skLineSegment(sketch, "E297.MirrorCS", {"start": v(-171.45, 71.45) * mm, "end": v(-171.45, 69.05) * mm});
            skLineSegment(sketch, "E298.MirrorCS", {"start": v(-173.25, 74.45) * mm, "end": v(-173.25, 71.45) * mm});
            skPoint(sketch, "E299.MirrorP", {"position": v(-172.75, 62.35) * mm});
            skPoint(sketch, "E300.MirrorP", {"position": v(-173.25, 75.95) * mm});
            skPoint(sketch, "E301.MirrorP", {"position": v(-172.75, 69.55) * mm});
            skLineSegment(sketch, "E302.MirrorCS", {"start": v(-167.74, 69.38) * mm, "end": v(-169.81, 71.45) * mm});
            skLineSegment(sketch, "E303.MirrorCS", {"start": v(-171.45, 71.45) * mm, "end": v(-169.81, 71.45) * mm});
            skLineSegment(sketch, "E304.MirrorCS", {"start": v(-173.25, 57.45) * mm, "end": v(-173.25, 62.35) * mm});
            skLineSegment(sketch, "E305.MirrorCS", {"start": v(-171.75, 55.95) * mm, "end": v(-168.75, 55.95) * mm});
            skPoint(sketch, "E306.MirrorP", {"position": v(-167.15, 69.85) * mm});
            skPoint(sketch, "E307.MirrorP", {"position": v(-166.09, 69.85) * mm});
            skLineSegment(sketch, "E308.MirrorCS", {"start": v(-168.75, 57.75) * mm, "end": v(-168.75, 59.4) * mm});
            skSolve(sketch);
        }
        {
            var Q0;
            Q0=makeQuery(id+"F4.imprint","IMPRINT",FACE,{"disambiguationData":[TD([[makeQuery(id+"F4.imprint","IMPRINT",EDGE,{"derivedFrom":sQuery(id+"F4.wireOp",EDGE,"E207.bottom")}),-1.0]])]});
            extrude(context, id + "F5", {"entities" : qUnion([Q0]), "depth" : 60 * mm, "offsetDistance" : 25 * mm});
        }
        {
            var Q0;
            Q0=qCreatedBy(makeId("Top.planeOp"),FACE);
            var sketch = newSketch(context, id + "F6", { "sketchPlane" : qUnion([Q0])});
            skCircle(sketch, "E309", {"center": v(-149.27, 9.98) * mm, "radius": 2.5 * mm});
            skLineSegment(sketch, "E310.bottom", {"start": v(-140.77, -0.02) * mm, "end": v(-145.17, -0.02) * mm});
            skLineSegment(sketch, "E310.top", {"start": v(-140.77, 19.98) * mm, "end": v(-145.17, 19.98) * mm});
            skLineSegment(sketch, "E310.left", {"start": v(-139.27, 1.48) * mm, "end": v(-139.27, 6.38) * mm});
            skLineSegment(sketch, "E311.bottom", {"start": v(-147.26, 6.08) * mm, "end": v(-151.28, 6.08) * mm});
            skLineSegment(sketch, "E311.top", {"start": v(-147.26, 13.88) * mm, "end": v(-151.28, 13.88) * mm});
            skLineSegment(sketch, "E311.left", {"start": v(-145.37, 7.97) * mm, "end": v(-145.37, 11.99) * mm});
            skLineSegment(sketch, "E311.right", {"start": v(-153.17, 7.97) * mm, "end": v(-153.17, 11.99) * mm});
            skLineSegment(sketch, "E312.bottom", {"start": v(-140.77, 19.98) * mm, "end": v(-143.77, 19.98) * mm});
            skLineSegment(sketch, "E312.left", {"start": v(-139.27, 18.48) * mm, "end": v(-139.27, 15.48) * mm});
            skLineSegment(sketch, "E312.right", {"start": v(-143.77, 18.18) * mm, "end": v(-143.77, 16.54) * mm});
            skLineSegment(sketch, "E313", {"start": v(-144.78, 13.4) * mm, "end": v(-142.7, 15.48) * mm});
            skLineSegment(sketch, "E314.MirrorCS", {"start": v(-145.84, 14.46) * mm, "end": v(-143.77, 16.54) * mm});
            skLineSegment(sketch, "E315", {"start": v(-141.07, 15.48) * mm, "end": v(-141.07, 13.08) * mm});
            skLineSegment(sketch, "E316", {"start": v(-139.57, 13.58) * mm, "end": v(-139.27, 13.58) * mm});
            skLineSegment(sketch, "E317", {"start": v(-141.07, 13.08) * mm, "end": v(-139.77, 13.08) * mm});
            skLineSegment(sketch, "E318", {"start": v(-139.77, 13.38) * mm, "end": v(-139.77, 13.08) * mm});
            skPoint(sketch, "E319.visualSharp", {"position": v(-139.77, 13.58) * mm});
            skArc(sketch, "E319.filletArc", {"start": v(-139.57, 13.58) * mm, "mid": v(-139.7, 13.52) * mm, "end": v(-139.77, 13.38) * mm});
            skPoint(sketch, "E320.newPointA", {"position": v(-145.37, 12.82) * mm});
            skArc(sketch, "E320.filletArc", {"start": v(-144.78, 13.4) * mm, "mid": v(-145.22, 12.75) * mm, "end": v(-145.37, 11.99) * mm});
            skPoint(sketch, "E321.newPointA", {"position": v(-146.43, 13.88) * mm});
            skPoint(sketch, "E321.newPointB", {"position": v(-145.37, 13.88) * mm});
            skArc(sketch, "E321.filletArc", {"start": v(-147.26, 13.88) * mm, "mid": v(-146.5, 14.03) * mm, "end": v(-145.84, 14.46) * mm});
            skLineSegment(sketch, "E322.MirrorCS", {"start": v(-143.77, 18.18) * mm, "end": v(-146.17, 18.18) * mm});
            skLineSegment(sketch, "E323.MirrorCS", {"start": v(-146.17, 18.18) * mm, "end": v(-146.17, 19.48) * mm});
            skPoint(sketch, "E324.visualSharp", {"position": v(-139.27, 19.98) * mm});
            skArc(sketch, "E324.filletArc", {"start": v(-139.27, 18.48) * mm, "mid": v(-139.7, 19.54) * mm, "end": v(-140.77, 19.98) * mm});
            skLineSegment(sketch, "E325.trimOffspring", {"start": v(-141.07, 15.48) * mm, "end": v(-142.7, 15.48) * mm});
            skLineSegment(sketch, "E326.MirrorCS", {"start": v(-139.57, 6.38) * mm, "end": v(-139.27, 6.38) * mm});
            skArc(sketch, "E327.MirrorCS", {"start": v(-139.57, 6.38) * mm, "mid": v(-139.7, 6.44) * mm, "end": v(-139.77, 6.58) * mm});
            skLineSegment(sketch, "E328.MirrorCS", {"start": v(-139.77, 6.58) * mm, "end": v(-139.77, 6.88) * mm});
            skArc(sketch, "E329.MirrorCS", {"start": v(-144.78, 6.55) * mm, "mid": v(-145.22, 7.2) * mm, "end": v(-145.37, 7.97) * mm});
            skLineSegment(sketch, "E330.MirrorCS", {"start": v(-141.07, 4.48) * mm, "end": v(-142.7, 4.48) * mm});
            skLineSegment(sketch, "E331.MirrorCS", {"start": v(-141.07, 6.88) * mm, "end": v(-139.77, 6.88) * mm});
            skLineSegment(sketch, "E332.MirrorCS", {"start": v(-140.77, -0.02) * mm, "end": v(-143.77, -0.02) * mm});
            skPoint(sketch, "E333.MirrorP", {"position": v(-139.77, 6.38) * mm});
            skLineSegment(sketch, "E334.MirrorCS", {"start": v(-146.17, 1.78) * mm, "end": v(-146.17, 0.48) * mm});
            skLineSegment(sketch, "E335.MirrorCS", {"start": v(-143.77, 1.78) * mm, "end": v(-146.17, 1.78) * mm});
            skLineSegment(sketch, "E336.MirrorCS", {"start": v(-141.07, 4.48) * mm, "end": v(-141.07, 6.88) * mm});
            skLineSegment(sketch, "E337.MirrorCS", {"start": v(-139.27, 1.48) * mm, "end": v(-139.27, 4.48) * mm});
            skLineSegment(sketch, "E338.MirrorCS", {"start": v(-144.78, 6.55) * mm, "end": v(-142.7, 4.48) * mm});
            skPoint(sketch, "E339.MirrorP", {"position": v(-145.37, 7.14) * mm});
            skPoint(sketch, "E340.MirrorP", {"position": v(-139.27, -0.02) * mm});
            skPoint(sketch, "E341.MirrorP", {"position": v(-145.37, 6.08) * mm});
            skLineSegment(sketch, "E342.MirrorCS", {"start": v(-145.84, 5.5) * mm, "end": v(-143.77, 3.42) * mm});
            skPoint(sketch, "E343.MirrorP", {"position": v(-146.43, 6.08) * mm});
            skArc(sketch, "E344.MirrorCS", {"start": v(-139.27, 1.48) * mm, "mid": v(-139.7, 0.42) * mm, "end": v(-140.77, -0.02) * mm});
            skLineSegment(sketch, "E345.MirrorCS", {"start": v(-143.77, 1.78) * mm, "end": v(-143.77, 3.42) * mm});
            skArc(sketch, "E346.MirrorCS", {"start": v(-147.26, 6.08) * mm, "mid": v(-146.5, 5.93) * mm, "end": v(-145.84, 5.5) * mm});
            skLineSegment(sketch, "E347.trimOffspring", {"start": v(-139.27, 13.58) * mm, "end": v(-139.27, 18.48) * mm});
            skLineSegment(sketch, "E348.MirrorCS", {"start": v(-145.67, 19.68) * mm, "end": v(-145.67, 19.98) * mm});
            skArc(sketch, "E349.MirrorCS", {"start": v(-145.67, 19.68) * mm, "mid": v(-145.73, 19.54) * mm, "end": v(-145.87, 19.48) * mm});
            skLineSegment(sketch, "E350.MirrorCS", {"start": v(-145.87, 19.48) * mm, "end": v(-146.17, 19.48) * mm});
            skLineSegment(sketch, "E351", {"start": v(-145.17, 19.98) * mm, "end": v(-145.67, 19.98) * mm});
            skLineSegment(sketch, "E352.MirrorCS", {"start": v(-145.67, 0.28) * mm, "end": v(-145.67, -0.02) * mm});
            skLineSegment(sketch, "E353.MirrorCS", {"start": v(-145.87, 0.48) * mm, "end": v(-146.17, 0.48) * mm});
            skLineSegment(sketch, "E354.MirrorCS", {"start": v(-145.17, -0.02) * mm, "end": v(-145.67, -0.02) * mm});
            skArc(sketch, "E355.MirrorCS", {"start": v(-145.67, 0.28) * mm, "mid": v(-145.73, 0.42) * mm, "end": v(-145.87, 0.48) * mm});
            skArc(sketch, "E356.MirrorCS", {"start": v(-158.97, 6.38) * mm, "mid": v(-158.83, 6.44) * mm, "end": v(-158.77, 6.58) * mm});
            skLineSegment(sketch, "E357.MirrorCS", {"start": v(-158.97, 13.58) * mm, "end": v(-159.27, 13.58) * mm});
            skLineSegment(sketch, "E358.MirrorCS", {"start": v(-158.77, 6.58) * mm, "end": v(-158.77, 6.88) * mm});
            skArc(sketch, "E359.MirrorCS", {"start": v(-158.97, 13.58) * mm, "mid": v(-158.83, 13.52) * mm, "end": v(-158.77, 13.38) * mm});
            skLineSegment(sketch, "E360.MirrorCS", {"start": v(-158.77, 13.38) * mm, "end": v(-158.77, 13.08) * mm});
            skLineSegment(sketch, "E361.MirrorCS", {"start": v(-158.97, 6.38) * mm, "end": v(-159.27, 6.38) * mm});
            skLineSegment(sketch, "E362.MirrorCS", {"start": v(-153.37, 19.98) * mm, "end": v(-152.87, 19.98) * mm});
            skArc(sketch, "E363.MirrorCS", {"start": v(-159.27, 1.48) * mm, "mid": v(-158.83, 0.42) * mm, "end": v(-157.77, -0.02) * mm});
            skLineSegment(sketch, "E364.MirrorCS", {"start": v(-152.87, 19.68) * mm, "end": v(-152.87, 19.98) * mm});
            skArc(sketch, "E365.MirrorCS", {"start": v(-153.75, 13.4) * mm, "mid": v(-153.32, 12.75) * mm, "end": v(-153.17, 11.99) * mm});
            skLineSegment(sketch, "E366.MirrorCS", {"start": v(-152.67, 0.48) * mm, "end": v(-152.37, 0.48) * mm});
            skLineSegment(sketch, "E367.MirrorCS", {"start": v(-152.37, 18.18) * mm, "end": v(-152.37, 19.48) * mm});
            skLineSegment(sketch, "E368.MirrorCS", {"start": v(-151.28, 13.88) * mm, "end": v(-147.26, 13.88) * mm});
            skLineSegment(sketch, "E369.MirrorCS", {"start": v(-157.47, 6.88) * mm, "end": v(-158.77, 6.88) * mm});
            skLineSegment(sketch, "E370.MirrorCS", {"start": v(-157.47, 13.08) * mm, "end": v(-158.77, 13.08) * mm});
            skLineSegment(sketch, "E371.MirrorCS", {"start": v(-152.67, 19.48) * mm, "end": v(-152.37, 19.48) * mm});
            skArc(sketch, "E372.MirrorCS", {"start": v(-153.75, 6.55) * mm, "mid": v(-153.32, 7.2) * mm, "end": v(-153.17, 7.97) * mm});
            skArc(sketch, "E373.MirrorCS", {"start": v(-152.87, 0.28) * mm, "mid": v(-152.8, 0.42) * mm, "end": v(-152.67, 0.48) * mm});
            skArc(sketch, "E374.MirrorCS", {"start": v(-152.87, 19.68) * mm, "mid": v(-152.8, 19.54) * mm, "end": v(-152.67, 19.48) * mm});
            skLineSegment(sketch, "E375.MirrorCS", {"start": v(-152.87, 0.28) * mm, "end": v(-152.87, -0.02) * mm});
            skLineSegment(sketch, "E376.MirrorCS", {"start": v(-151.28, 6.08) * mm, "end": v(-147.26, 6.08) * mm});
            skLineSegment(sketch, "E377.MirrorCS", {"start": v(-153.37, -0.02) * mm, "end": v(-152.87, -0.02) * mm});
            skLineSegment(sketch, "E378.MirrorCS", {"start": v(-152.37, 1.78) * mm, "end": v(-152.37, 0.48) * mm});
            skArc(sketch, "E379.MirrorCS", {"start": v(-151.28, 13.88) * mm, "mid": v(-152.04, 14.03) * mm, "end": v(-152.7, 14.46) * mm});
            skPoint(sketch, "E380.MirrorP", {"position": v(-159.27, -0.02) * mm});
            skLineSegment(sketch, "E381.MirrorCS", {"start": v(-157.77, -0.02) * mm, "end": v(-153.37, -0.02) * mm});
            skPoint(sketch, "E382.MirrorP", {"position": v(-153.17, 6.08) * mm});
            skLineSegment(sketch, "E383.MirrorCS", {"start": v(-157.77, 19.98) * mm, "end": v(-153.37, 19.98) * mm});
            skArc(sketch, "E384.MirrorCS", {"start": v(-151.28, 6.08) * mm, "mid": v(-152.04, 5.93) * mm, "end": v(-152.7, 5.5) * mm});
            skArc(sketch, "E385.MirrorCS", {"start": v(-159.27, 18.48) * mm, "mid": v(-158.83, 19.54) * mm, "end": v(-157.77, 19.98) * mm});
            skPoint(sketch, "E386.MirrorP", {"position": v(-153.17, 7.14) * mm});
            skLineSegment(sketch, "E387.MirrorCS", {"start": v(-154.77, 18.18) * mm, "end": v(-154.77, 16.54) * mm});
            skLineSegment(sketch, "E388.MirrorCS", {"start": v(-152.7, 14.46) * mm, "end": v(-154.77, 16.54) * mm});
            skPoint(sketch, "E389.MirrorP", {"position": v(-153.17, 12.82) * mm});
            skLineSegment(sketch, "E390.MirrorCS", {"start": v(-157.47, 4.48) * mm, "end": v(-157.47, 6.88) * mm});
            skLineSegment(sketch, "E391.MirrorCS", {"start": v(-153.75, 6.55) * mm, "end": v(-155.83, 4.48) * mm});
            skLineSegment(sketch, "E392.MirrorCS", {"start": v(-154.77, 1.78) * mm, "end": v(-152.37, 1.78) * mm});
            skLineSegment(sketch, "E393.MirrorCS", {"start": v(-157.47, 4.48) * mm, "end": v(-155.83, 4.48) * mm});
            skLineSegment(sketch, "E394.MirrorCS", {"start": v(-159.27, 1.48) * mm, "end": v(-159.27, 4.48) * mm});
            skLineSegment(sketch, "E395.MirrorCS", {"start": v(-157.77, 19.98) * mm, "end": v(-154.77, 19.98) * mm});
            skLineSegment(sketch, "E396.MirrorCS", {"start": v(-159.27, 13.58) * mm, "end": v(-159.27, 18.48) * mm});
            skLineSegment(sketch, "E397.MirrorCS", {"start": v(-154.77, 18.18) * mm, "end": v(-152.37, 18.18) * mm});
            skLineSegment(sketch, "E398.MirrorCS", {"start": v(-152.7, 5.5) * mm, "end": v(-154.77, 3.42) * mm});
            skPoint(sketch, "E399.MirrorP", {"position": v(-152.1, 6.08) * mm});
            skLineSegment(sketch, "E400.MirrorCS", {"start": v(-157.47, 15.48) * mm, "end": v(-157.47, 13.08) * mm});
            skLineSegment(sketch, "E401.MirrorCS", {"start": v(-159.27, 18.48) * mm, "end": v(-159.27, 15.48) * mm});
            skPoint(sketch, "E402.MirrorP", {"position": v(-158.77, 6.38) * mm});
            skPoint(sketch, "E403.MirrorP", {"position": v(-159.27, 19.98) * mm});
            skPoint(sketch, "E404.MirrorP", {"position": v(-158.77, 13.58) * mm});
            skLineSegment(sketch, "E405.MirrorCS", {"start": v(-153.75, 13.4) * mm, "end": v(-155.83, 15.48) * mm});
            skLineSegment(sketch, "E406.MirrorCS", {"start": v(-157.47, 15.48) * mm, "end": v(-155.83, 15.48) * mm});
            skLineSegment(sketch, "E407.MirrorCS", {"start": v(-159.27, 1.48) * mm, "end": v(-159.27, 6.38) * mm});
            skLineSegment(sketch, "E408.MirrorCS", {"start": v(-157.77, -0.02) * mm, "end": v(-154.77, -0.02) * mm});
            skPoint(sketch, "E409.MirrorP", {"position": v(-153.17, 13.88) * mm});
            skPoint(sketch, "E410.MirrorP", {"position": v(-152.1, 13.88) * mm});
            skLineSegment(sketch, "E411.MirrorCS", {"start": v(-154.77, 1.78) * mm, "end": v(-154.77, 3.42) * mm});
            skSolve(sketch);
        }
        {
            var Q0;
            Q0=makeQuery(id+"F6.imprint","IMPRINT",FACE,{"disambiguationData":[TD([[makeQuery(id+"F6.imprint","IMPRINT",EDGE,{"derivedFrom":sQuery(id+"F6.wireOp",EDGE,"E310.bottom")}),-1.0]])]});
            extrude(context, id + "F7", {"entities" : qUnion([Q0]), "depth" : 132 * mm, "offsetDistance" : 25 * mm});
        }
        {
            var Q0;
            Q0=qCreatedBy(makeId("Top.planeOp"),FACE);
            var sketch = newSketch(context, id + "F8", { "sketchPlane" : qUnion([Q0])});
            skCircle(sketch, "E412", {"center": v(-144.02, -34.35) * mm, "radius": 2.5 * mm});
            skLineSegment(sketch, "E413.bottom", {"start": v(-135.52, -44.35) * mm, "end": v(-139.92, -44.35) * mm});
            skLineSegment(sketch, "E413.top", {"start": v(-135.52, -24.35) * mm, "end": v(-139.92, -24.35) * mm});
            skLineSegment(sketch, "E413.left", {"start": v(-134.02, -42.85) * mm, "end": v(-134.02, -37.95) * mm});
            skLineSegment(sketch, "E414.bottom", {"start": v(-142, -38.25) * mm, "end": v(-146.03, -38.25) * mm});
            skLineSegment(sketch, "E414.top", {"start": v(-142, -30.45) * mm, "end": v(-146.03, -30.45) * mm});
            skLineSegment(sketch, "E414.left", {"start": v(-140.12, -36.37) * mm, "end": v(-140.12, -32.34) * mm});
            skLineSegment(sketch, "E414.right", {"start": v(-147.92, -36.37) * mm, "end": v(-147.92, -32.34) * mm});
            skLineSegment(sketch, "E415.bottom", {"start": v(-135.52, -24.35) * mm, "end": v(-138.52, -24.35) * mm});
            skLineSegment(sketch, "E415.left", {"start": v(-134.02, -25.85) * mm, "end": v(-134.02, -28.85) * mm});
            skLineSegment(sketch, "E415.right", {"start": v(-138.52, -26.15) * mm, "end": v(-138.52, -27.8) * mm});
            skLineSegment(sketch, "E416", {"start": v(-139.53, -30.93) * mm, "end": v(-137.46, -28.85) * mm});
            skLineSegment(sketch, "E417.MirrorCS", {"start": v(-140.6, -29.87) * mm, "end": v(-138.52, -27.8) * mm});
            skLineSegment(sketch, "E418", {"start": v(-135.82, -28.85) * mm, "end": v(-135.82, -31.25) * mm});
            skLineSegment(sketch, "E419", {"start": v(-134.32, -30.75) * mm, "end": v(-134.02, -30.75) * mm});
            skLineSegment(sketch, "E420", {"start": v(-135.82, -31.25) * mm, "end": v(-134.52, -31.25) * mm});
            skLineSegment(sketch, "E421", {"start": v(-134.52, -30.95) * mm, "end": v(-134.52, -31.25) * mm});
            skPoint(sketch, "E422.visualSharp", {"position": v(-134.52, -30.75) * mm});
            skArc(sketch, "E422.filletArc", {"start": v(-134.32, -30.75) * mm, "mid": v(-134.46, -30.81) * mm, "end": v(-134.52, -30.95) * mm});
            skPoint(sketch, "E423.newPointA", {"position": v(-140.12, -31.51) * mm});
            skArc(sketch, "E423.filletArc", {"start": v(-139.53, -30.93) * mm, "mid": v(-139.97, -31.58) * mm, "end": v(-140.12, -32.34) * mm});
            skPoint(sketch, "E424.newPointA", {"position": v(-141.18, -30.45) * mm});
            skPoint(sketch, "E424.newPointB", {"position": v(-140.12, -30.45) * mm});
            skArc(sketch, "E424.filletArc", {"start": v(-142, -30.45) * mm, "mid": v(-141.24, -30.3) * mm, "end": v(-140.6, -29.87) * mm});
            skLineSegment(sketch, "E425.MirrorCS", {"start": v(-138.52, -26.15) * mm, "end": v(-140.92, -26.15) * mm});
            skLineSegment(sketch, "E426.MirrorCS", {"start": v(-140.92, -26.15) * mm, "end": v(-140.92, -24.85) * mm});
            skPoint(sketch, "E427.visualSharp", {"position": v(-134.02, -24.35) * mm});
            skArc(sketch, "E427.filletArc", {"start": v(-134.02, -25.85) * mm, "mid": v(-134.46, -24.8) * mm, "end": v(-135.52, -24.35) * mm});
            skLineSegment(sketch, "E428.trimOffspring", {"start": v(-135.82, -28.85) * mm, "end": v(-137.46, -28.85) * mm});
            skLineSegment(sketch, "E429.MirrorCS", {"start": v(-134.32, -37.95) * mm, "end": v(-134.02, -37.95) * mm});
            skArc(sketch, "E430.MirrorCS", {"start": v(-134.32, -37.95) * mm, "mid": v(-134.46, -37.9) * mm, "end": v(-134.52, -37.75) * mm});
            skLineSegment(sketch, "E431.MirrorCS", {"start": v(-134.52, -37.75) * mm, "end": v(-134.52, -37.45) * mm});
            skArc(sketch, "E432.MirrorCS", {"start": v(-139.53, -37.78) * mm, "mid": v(-139.97, -37.13) * mm, "end": v(-140.12, -36.37) * mm});
            skLineSegment(sketch, "E433.MirrorCS", {"start": v(-135.82, -39.85) * mm, "end": v(-137.46, -39.85) * mm});
            skLineSegment(sketch, "E434.MirrorCS", {"start": v(-135.82, -37.45) * mm, "end": v(-134.52, -37.45) * mm});
            skLineSegment(sketch, "E435.MirrorCS", {"start": v(-135.52, -44.35) * mm, "end": v(-138.52, -44.35) * mm});
            skPoint(sketch, "E436.MirrorP", {"position": v(-134.52, -37.95) * mm});
            skLineSegment(sketch, "E437.MirrorCS", {"start": v(-140.92, -42.55) * mm, "end": v(-140.92, -43.85) * mm});
            skLineSegment(sketch, "E438.MirrorCS", {"start": v(-138.52, -42.55) * mm, "end": v(-140.92, -42.55) * mm});
            skLineSegment(sketch, "E439.MirrorCS", {"start": v(-135.82, -39.85) * mm, "end": v(-135.82, -37.45) * mm});
            skLineSegment(sketch, "E440.MirrorCS", {"start": v(-134.02, -42.85) * mm, "end": v(-134.02, -39.85) * mm});
            skLineSegment(sketch, "E441.MirrorCS", {"start": v(-139.53, -37.78) * mm, "end": v(-137.46, -39.85) * mm});
            skPoint(sketch, "E442.MirrorP", {"position": v(-140.12, -37.2) * mm});
            skPoint(sketch, "E443.MirrorP", {"position": v(-134.02, -44.35) * mm});
            skPoint(sketch, "E444.MirrorP", {"position": v(-140.12, -38.25) * mm});
            skLineSegment(sketch, "E445.MirrorCS", {"start": v(-140.6, -38.84) * mm, "end": v(-138.52, -40.91) * mm});
            skPoint(sketch, "E446.MirrorP", {"position": v(-141.18, -38.25) * mm});
            skArc(sketch, "E447.MirrorCS", {"start": v(-134.02, -42.85) * mm, "mid": v(-134.46, -43.91) * mm, "end": v(-135.52, -44.35) * mm});
            skLineSegment(sketch, "E448.MirrorCS", {"start": v(-138.52, -42.55) * mm, "end": v(-138.52, -40.91) * mm});
            skArc(sketch, "E449.MirrorCS", {"start": v(-142, -38.25) * mm, "mid": v(-141.24, -38.4) * mm, "end": v(-140.6, -38.84) * mm});
            skLineSegment(sketch, "E450.trimOffspring", {"start": v(-134.02, -30.75) * mm, "end": v(-134.02, -25.85) * mm});
            skLineSegment(sketch, "E451.MirrorCS", {"start": v(-140.42, -24.65) * mm, "end": v(-140.42, -24.35) * mm});
            skArc(sketch, "E452.MirrorCS", {"start": v(-140.42, -24.65) * mm, "mid": v(-140.48, -24.8) * mm, "end": v(-140.62, -24.85) * mm});
            skLineSegment(sketch, "E453.MirrorCS", {"start": v(-140.62, -24.85) * mm, "end": v(-140.92, -24.85) * mm});
            skLineSegment(sketch, "E454", {"start": v(-139.92, -24.35) * mm, "end": v(-140.42, -24.35) * mm});
            skLineSegment(sketch, "E455.MirrorCS", {"start": v(-140.42, -44.05) * mm, "end": v(-140.42, -44.35) * mm});
            skLineSegment(sketch, "E456.MirrorCS", {"start": v(-140.62, -43.85) * mm, "end": v(-140.92, -43.85) * mm});
            skLineSegment(sketch, "E457.MirrorCS", {"start": v(-139.92, -44.35) * mm, "end": v(-140.42, -44.35) * mm});
            skArc(sketch, "E458.MirrorCS", {"start": v(-140.42, -44.05) * mm, "mid": v(-140.48, -43.91) * mm, "end": v(-140.62, -43.85) * mm});
            skArc(sketch, "E459.MirrorCS", {"start": v(-153.72, -37.95) * mm, "mid": v(-153.58, -37.9) * mm, "end": v(-153.52, -37.75) * mm});
            skLineSegment(sketch, "E460.MirrorCS", {"start": v(-153.72, -30.75) * mm, "end": v(-154.02, -30.75) * mm});
            skLineSegment(sketch, "E461.MirrorCS", {"start": v(-153.52, -37.75) * mm, "end": v(-153.52, -37.45) * mm});
            skArc(sketch, "E462.MirrorCS", {"start": v(-153.72, -30.75) * mm, "mid": v(-153.58, -30.81) * mm, "end": v(-153.52, -30.95) * mm});
            skLineSegment(sketch, "E463.MirrorCS", {"start": v(-153.52, -30.95) * mm, "end": v(-153.52, -31.25) * mm});
            skLineSegment(sketch, "E464.MirrorCS", {"start": v(-153.72, -37.95) * mm, "end": v(-154.02, -37.95) * mm});
            skLineSegment(sketch, "E465.MirrorCS", {"start": v(-148.12, -24.35) * mm, "end": v(-147.62, -24.35) * mm});
            skArc(sketch, "E466.MirrorCS", {"start": v(-154.02, -42.85) * mm, "mid": v(-153.58, -43.91) * mm, "end": v(-152.52, -44.35) * mm});
            skLineSegment(sketch, "E467.MirrorCS", {"start": v(-147.62, -24.65) * mm, "end": v(-147.62, -24.35) * mm});
            skArc(sketch, "E468.MirrorCS", {"start": v(-148.5, -30.93) * mm, "mid": v(-148.07, -31.58) * mm, "end": v(-147.92, -32.34) * mm});
            skLineSegment(sketch, "E469.MirrorCS", {"start": v(-147.42, -43.85) * mm, "end": v(-147.12, -43.85) * mm});
            skLineSegment(sketch, "E470.MirrorCS", {"start": v(-147.12, -26.15) * mm, "end": v(-147.12, -24.85) * mm});
            skLineSegment(sketch, "E471.MirrorCS", {"start": v(-146.03, -30.45) * mm, "end": v(-142, -30.45) * mm});
            skLineSegment(sketch, "E472.MirrorCS", {"start": v(-152.22, -37.45) * mm, "end": v(-153.52, -37.45) * mm});
            skLineSegment(sketch, "E473.MirrorCS", {"start": v(-152.22, -31.25) * mm, "end": v(-153.52, -31.25) * mm});
            skLineSegment(sketch, "E474.MirrorCS", {"start": v(-147.42, -24.85) * mm, "end": v(-147.12, -24.85) * mm});
            skArc(sketch, "E475.MirrorCS", {"start": v(-148.5, -37.78) * mm, "mid": v(-148.07, -37.13) * mm, "end": v(-147.92, -36.37) * mm});
            skArc(sketch, "E476.MirrorCS", {"start": v(-147.62, -44.05) * mm, "mid": v(-147.56, -43.91) * mm, "end": v(-147.42, -43.85) * mm});
            skArc(sketch, "E477.MirrorCS", {"start": v(-147.62, -24.65) * mm, "mid": v(-147.56, -24.8) * mm, "end": v(-147.42, -24.85) * mm});
            skLineSegment(sketch, "E478.MirrorCS", {"start": v(-147.62, -44.05) * mm, "end": v(-147.62, -44.35) * mm});
            skLineSegment(sketch, "E479.MirrorCS", {"start": v(-146.03, -38.25) * mm, "end": v(-142, -38.25) * mm});
            skLineSegment(sketch, "E480.MirrorCS", {"start": v(-148.12, -44.35) * mm, "end": v(-147.62, -44.35) * mm});
            skLineSegment(sketch, "E481.MirrorCS", {"start": v(-147.12, -42.55) * mm, "end": v(-147.12, -43.85) * mm});
            skArc(sketch, "E482.MirrorCS", {"start": v(-146.03, -30.45) * mm, "mid": v(-146.8, -30.3) * mm, "end": v(-147.44, -29.87) * mm});
            skPoint(sketch, "E483.MirrorP", {"position": v(-154.02, -44.35) * mm});
            skLineSegment(sketch, "E484.MirrorCS", {"start": v(-152.52, -44.35) * mm, "end": v(-148.12, -44.35) * mm});
            skPoint(sketch, "E485.MirrorP", {"position": v(-147.92, -38.25) * mm});
            skLineSegment(sketch, "E486.MirrorCS", {"start": v(-152.52, -24.35) * mm, "end": v(-148.12, -24.35) * mm});
            skArc(sketch, "E487.MirrorCS", {"start": v(-146.03, -38.25) * mm, "mid": v(-146.8, -38.4) * mm, "end": v(-147.44, -38.84) * mm});
            skArc(sketch, "E488.MirrorCS", {"start": v(-154.02, -25.85) * mm, "mid": v(-153.58, -24.8) * mm, "end": v(-152.52, -24.35) * mm});
            skPoint(sketch, "E489.MirrorP", {"position": v(-147.92, -37.2) * mm});
            skLineSegment(sketch, "E490.MirrorCS", {"start": v(-149.52, -26.15) * mm, "end": v(-149.52, -27.8) * mm});
            skLineSegment(sketch, "E491.MirrorCS", {"start": v(-147.44, -29.87) * mm, "end": v(-149.52, -27.8) * mm});
            skPoint(sketch, "E492.MirrorP", {"position": v(-147.92, -31.51) * mm});
            skLineSegment(sketch, "E493.MirrorCS", {"start": v(-152.22, -39.85) * mm, "end": v(-152.22, -37.45) * mm});
            skLineSegment(sketch, "E494.MirrorCS", {"start": v(-148.5, -37.78) * mm, "end": v(-150.58, -39.85) * mm});
            skLineSegment(sketch, "E495.MirrorCS", {"start": v(-149.52, -42.55) * mm, "end": v(-147.12, -42.55) * mm});
            skLineSegment(sketch, "E496.MirrorCS", {"start": v(-152.22, -39.85) * mm, "end": v(-150.58, -39.85) * mm});
            skLineSegment(sketch, "E497.MirrorCS", {"start": v(-154.02, -42.85) * mm, "end": v(-154.02, -39.85) * mm});
            skLineSegment(sketch, "E498.MirrorCS", {"start": v(-152.52, -24.35) * mm, "end": v(-149.52, -24.35) * mm});
            skLineSegment(sketch, "E499.MirrorCS", {"start": v(-154.02, -30.75) * mm, "end": v(-154.02, -25.85) * mm});
            skLineSegment(sketch, "E500.MirrorCS", {"start": v(-149.52, -26.15) * mm, "end": v(-147.12, -26.15) * mm});
            skLineSegment(sketch, "E501.MirrorCS", {"start": v(-147.44, -38.84) * mm, "end": v(-149.52, -40.91) * mm});
            skPoint(sketch, "E502.MirrorP", {"position": v(-146.86, -38.25) * mm});
            skLineSegment(sketch, "E503.MirrorCS", {"start": v(-152.22, -28.85) * mm, "end": v(-152.22, -31.25) * mm});
            skLineSegment(sketch, "E504.MirrorCS", {"start": v(-154.02, -25.85) * mm, "end": v(-154.02, -28.85) * mm});
            skPoint(sketch, "E505.MirrorP", {"position": v(-153.52, -37.95) * mm});
            skPoint(sketch, "E506.MirrorP", {"position": v(-154.02, -24.35) * mm});
            skPoint(sketch, "E507.MirrorP", {"position": v(-153.52, -30.75) * mm});
            skLineSegment(sketch, "E508.MirrorCS", {"start": v(-148.5, -30.93) * mm, "end": v(-150.58, -28.85) * mm});
            skLineSegment(sketch, "E509.MirrorCS", {"start": v(-152.22, -28.85) * mm, "end": v(-150.58, -28.85) * mm});
            skLineSegment(sketch, "E510.MirrorCS", {"start": v(-154.02, -42.85) * mm, "end": v(-154.02, -37.95) * mm});
            skLineSegment(sketch, "E511.MirrorCS", {"start": v(-152.52, -44.35) * mm, "end": v(-149.52, -44.35) * mm});
            skPoint(sketch, "E512.MirrorP", {"position": v(-147.92, -30.45) * mm});
            skPoint(sketch, "E513.MirrorP", {"position": v(-146.86, -30.45) * mm});
            skLineSegment(sketch, "E514.MirrorCS", {"start": v(-149.52, -42.55) * mm, "end": v(-149.52, -40.91) * mm});
            skSolve(sketch);
        }
        {
            var Q0;
            Q0=makeQuery(id+"F8.imprint","IMPRINT",FACE,{"disambiguationData":[TD([[makeQuery(id+"F8.imprint","IMPRINT",EDGE,{"derivedFrom":sQuery(id+"F8.wireOp",EDGE,"E413.bottom")}),-1.0]])]});
            extrude(context, id + "F9", {"entities" : qUnion([Q0]), "depth" : 488 * mm, "offsetDistance" : 25 * mm});
        }
        {
            var Q0;
            Q0=qCreatedBy(makeId("Top.planeOp"),FACE);
            var sketch = newSketch(context, id + "F10", { "sketchPlane" : qUnion([Q0])});
            skCircle(sketch, "E515", {"center": v(-111.26, 55.19) * mm, "radius": 2.5 * mm});
            skLineSegment(sketch, "E516.bottom", {"start": v(-102.76, 45.19) * mm, "end": v(-107.16, 45.19) * mm});
            skLineSegment(sketch, "E516.top", {"start": v(-102.76, 65.19) * mm, "end": v(-107.16, 65.19) * mm});
            skLineSegment(sketch, "E516.left", {"start": v(-101.26, 46.69) * mm, "end": v(-101.26, 51.59) * mm});
            skLineSegment(sketch, "E517.bottom", {"start": v(-109.25, 51.29) * mm, "end": v(-113.27, 51.29) * mm});
            skLineSegment(sketch, "E517.top", {"start": v(-109.25, 59.09) * mm, "end": v(-113.27, 59.09) * mm});
            skLineSegment(sketch, "E517.left", {"start": v(-107.36, 53.18) * mm, "end": v(-107.36, 57.2) * mm});
            skLineSegment(sketch, "E517.right", {"start": v(-115.16, 53.18) * mm, "end": v(-115.16, 57.2) * mm});
            skLineSegment(sketch, "E518.bottom", {"start": v(-102.76, 65.19) * mm, "end": v(-105.76, 65.19) * mm});
            skLineSegment(sketch, "E518.left", {"start": v(-101.26, 63.69) * mm, "end": v(-101.26, 60.69) * mm});
            skLineSegment(sketch, "E518.right", {"start": v(-105.76, 63.39) * mm, "end": v(-105.76, 61.75) * mm});
            skLineSegment(sketch, "E519", {"start": v(-106.78, 58.61) * mm, "end": v(-104.7, 60.69) * mm});
            skLineSegment(sketch, "E520.MirrorCS", {"start": v(-107.84, 59.68) * mm, "end": v(-105.76, 61.75) * mm});
            skLineSegment(sketch, "E521", {"start": v(-103.06, 60.69) * mm, "end": v(-103.06, 58.29) * mm});
            skLineSegment(sketch, "E522", {"start": v(-101.56, 58.79) * mm, "end": v(-101.26, 58.79) * mm});
            skLineSegment(sketch, "E523", {"start": v(-103.06, 58.29) * mm, "end": v(-101.76, 58.29) * mm});
            skLineSegment(sketch, "E524", {"start": v(-101.76, 58.59) * mm, "end": v(-101.76, 58.29) * mm});
            skPoint(sketch, "E525.visualSharp", {"position": v(-101.76, 58.79) * mm});
            skArc(sketch, "E525.filletArc", {"start": v(-101.56, 58.79) * mm, "mid": v(-101.7, 58.73) * mm, "end": v(-101.76, 58.59) * mm});
            skPoint(sketch, "E526.newPointA", {"position": v(-107.36, 58.03) * mm});
            skArc(sketch, "E526.filletArc", {"start": v(-106.78, 58.61) * mm, "mid": v(-107.2, 57.97) * mm, "end": v(-107.36, 57.2) * mm});
            skPoint(sketch, "E527.newPointA", {"position": v(-108.42, 59.09) * mm});
            skPoint(sketch, "E527.newPointB", {"position": v(-107.36, 59.09) * mm});
            skArc(sketch, "E527.filletArc", {"start": v(-109.25, 59.09) * mm, "mid": v(-108.49, 59.24) * mm, "end": v(-107.84, 59.68) * mm});
            skLineSegment(sketch, "E528.MirrorCS", {"start": v(-105.76, 63.39) * mm, "end": v(-108.16, 63.39) * mm});
            skLineSegment(sketch, "E529.MirrorCS", {"start": v(-108.16, 63.39) * mm, "end": v(-108.16, 64.69) * mm});
            skPoint(sketch, "E530.visualSharp", {"position": v(-101.26, 65.19) * mm});
            skArc(sketch, "E530.filletArc", {"start": v(-101.26, 63.69) * mm, "mid": v(-101.7, 64.75) * mm, "end": v(-102.76, 65.19) * mm});
            skLineSegment(sketch, "E531.trimOffspring", {"start": v(-103.06, 60.69) * mm, "end": v(-104.7, 60.69) * mm});
            skLineSegment(sketch, "E532.MirrorCS", {"start": v(-101.56, 51.59) * mm, "end": v(-101.26, 51.59) * mm});
            skArc(sketch, "E533.MirrorCS", {"start": v(-101.56, 51.59) * mm, "mid": v(-101.7, 51.65) * mm, "end": v(-101.76, 51.79) * mm});
            skLineSegment(sketch, "E534.MirrorCS", {"start": v(-101.76, 51.79) * mm, "end": v(-101.76, 52.09) * mm});
            skArc(sketch, "E535.MirrorCS", {"start": v(-106.78, 51.76) * mm, "mid": v(-107.2, 52.41) * mm, "end": v(-107.36, 53.18) * mm});
            skLineSegment(sketch, "E536.MirrorCS", {"start": v(-103.06, 49.69) * mm, "end": v(-104.7, 49.69) * mm});
            skLineSegment(sketch, "E537.MirrorCS", {"start": v(-103.06, 52.09) * mm, "end": v(-101.76, 52.09) * mm});
            skLineSegment(sketch, "E538.MirrorCS", {"start": v(-102.76, 45.19) * mm, "end": v(-105.76, 45.19) * mm});
            skPoint(sketch, "E539.MirrorP", {"position": v(-101.76, 51.59) * mm});
            skLineSegment(sketch, "E540.MirrorCS", {"start": v(-108.16, 46.99) * mm, "end": v(-108.16, 45.69) * mm});
            skLineSegment(sketch, "E541.MirrorCS", {"start": v(-105.76, 46.99) * mm, "end": v(-108.16, 46.99) * mm});
            skLineSegment(sketch, "E542.MirrorCS", {"start": v(-103.06, 49.69) * mm, "end": v(-103.06, 52.09) * mm});
            skLineSegment(sketch, "E543.MirrorCS", {"start": v(-101.26, 46.69) * mm, "end": v(-101.26, 49.69) * mm});
            skLineSegment(sketch, "E544.MirrorCS", {"start": v(-106.78, 51.76) * mm, "end": v(-104.7, 49.69) * mm});
            skPoint(sketch, "E545.MirrorP", {"position": v(-107.36, 52.35) * mm});
            skPoint(sketch, "E546.MirrorP", {"position": v(-101.26, 45.19) * mm});
            skPoint(sketch, "E547.MirrorP", {"position": v(-107.36, 51.29) * mm});
            skLineSegment(sketch, "E548.MirrorCS", {"start": v(-107.84, 50.7) * mm, "end": v(-105.76, 48.63) * mm});
            skPoint(sketch, "E549.MirrorP", {"position": v(-108.42, 51.29) * mm});
            skArc(sketch, "E550.MirrorCS", {"start": v(-101.26, 46.69) * mm, "mid": v(-101.7, 45.63) * mm, "end": v(-102.76, 45.19) * mm});
            skLineSegment(sketch, "E551.MirrorCS", {"start": v(-105.76, 46.99) * mm, "end": v(-105.76, 48.63) * mm});
            skArc(sketch, "E552.MirrorCS", {"start": v(-109.25, 51.29) * mm, "mid": v(-108.49, 51.14) * mm, "end": v(-107.84, 50.7) * mm});
            skLineSegment(sketch, "E553.trimOffspring", {"start": v(-101.26, 58.79) * mm, "end": v(-101.26, 63.69) * mm});
            skLineSegment(sketch, "E554.MirrorCS", {"start": v(-107.66, 64.89) * mm, "end": v(-107.66, 65.19) * mm});
            skArc(sketch, "E555.MirrorCS", {"start": v(-107.66, 64.89) * mm, "mid": v(-107.72, 64.75) * mm, "end": v(-107.86, 64.69) * mm});
            skLineSegment(sketch, "E556.MirrorCS", {"start": v(-107.86, 64.69) * mm, "end": v(-108.16, 64.69) * mm});
            skLineSegment(sketch, "E557", {"start": v(-107.16, 65.19) * mm, "end": v(-107.66, 65.19) * mm});
            skLineSegment(sketch, "E558.MirrorCS", {"start": v(-107.66, 45.49) * mm, "end": v(-107.66, 45.19) * mm});
            skLineSegment(sketch, "E559.MirrorCS", {"start": v(-107.86, 45.69) * mm, "end": v(-108.16, 45.69) * mm});
            skLineSegment(sketch, "E560.MirrorCS", {"start": v(-107.16, 45.19) * mm, "end": v(-107.66, 45.19) * mm});
            skArc(sketch, "E561.MirrorCS", {"start": v(-107.66, 45.49) * mm, "mid": v(-107.72, 45.63) * mm, "end": v(-107.86, 45.69) * mm});
            skArc(sketch, "E562.MirrorCS", {"start": v(-120.96, 51.59) * mm, "mid": v(-120.82, 51.65) * mm, "end": v(-120.76, 51.79) * mm});
            skLineSegment(sketch, "E563.MirrorCS", {"start": v(-120.96, 58.79) * mm, "end": v(-121.26, 58.79) * mm});
            skLineSegment(sketch, "E564.MirrorCS", {"start": v(-120.76, 51.79) * mm, "end": v(-120.76, 52.09) * mm});
            skArc(sketch, "E565.MirrorCS", {"start": v(-120.96, 58.79) * mm, "mid": v(-120.82, 58.73) * mm, "end": v(-120.76, 58.59) * mm});
            skLineSegment(sketch, "E566.MirrorCS", {"start": v(-120.76, 58.59) * mm, "end": v(-120.76, 58.29) * mm});
            skLineSegment(sketch, "E567.MirrorCS", {"start": v(-120.96, 51.59) * mm, "end": v(-121.26, 51.59) * mm});
            skLineSegment(sketch, "E568.MirrorCS", {"start": v(-115.36, 65.19) * mm, "end": v(-114.86, 65.19) * mm});
            skArc(sketch, "E569.MirrorCS", {"start": v(-121.26, 46.69) * mm, "mid": v(-120.82, 45.63) * mm, "end": v(-119.76, 45.19) * mm});
            skLineSegment(sketch, "E570.MirrorCS", {"start": v(-114.86, 64.89) * mm, "end": v(-114.86, 65.19) * mm});
            skArc(sketch, "E571.MirrorCS", {"start": v(-115.75, 58.61) * mm, "mid": v(-115.31, 57.97) * mm, "end": v(-115.16, 57.2) * mm});
            skLineSegment(sketch, "E572.MirrorCS", {"start": v(-114.66, 45.69) * mm, "end": v(-114.36, 45.69) * mm});
            skLineSegment(sketch, "E573.MirrorCS", {"start": v(-114.36, 63.39) * mm, "end": v(-114.36, 64.69) * mm});
            skLineSegment(sketch, "E574.MirrorCS", {"start": v(-113.27, 59.09) * mm, "end": v(-109.25, 59.09) * mm});
            skLineSegment(sketch, "E575.MirrorCS", {"start": v(-119.46, 52.09) * mm, "end": v(-120.76, 52.09) * mm});
            skLineSegment(sketch, "E576.MirrorCS", {"start": v(-119.46, 58.29) * mm, "end": v(-120.76, 58.29) * mm});
            skLineSegment(sketch, "E577.MirrorCS", {"start": v(-114.66, 64.69) * mm, "end": v(-114.36, 64.69) * mm});
            skArc(sketch, "E578.MirrorCS", {"start": v(-115.75, 51.76) * mm, "mid": v(-115.31, 52.41) * mm, "end": v(-115.16, 53.18) * mm});
            skArc(sketch, "E579.MirrorCS", {"start": v(-114.86, 45.49) * mm, "mid": v(-114.8, 45.63) * mm, "end": v(-114.66, 45.69) * mm});
            skArc(sketch, "E580.MirrorCS", {"start": v(-114.86, 64.89) * mm, "mid": v(-114.8, 64.75) * mm, "end": v(-114.66, 64.69) * mm});
            skLineSegment(sketch, "E581.MirrorCS", {"start": v(-114.86, 45.49) * mm, "end": v(-114.86, 45.19) * mm});
            skLineSegment(sketch, "E582.MirrorCS", {"start": v(-113.27, 51.29) * mm, "end": v(-109.25, 51.29) * mm});
            skLineSegment(sketch, "E583.MirrorCS", {"start": v(-115.36, 45.19) * mm, "end": v(-114.86, 45.19) * mm});
            skLineSegment(sketch, "E584.MirrorCS", {"start": v(-114.36, 46.99) * mm, "end": v(-114.36, 45.69) * mm});
            skArc(sketch, "E585.MirrorCS", {"start": v(-113.27, 59.09) * mm, "mid": v(-114.04, 59.24) * mm, "end": v(-114.69, 59.68) * mm});
            skPoint(sketch, "E586.MirrorP", {"position": v(-121.26, 45.19) * mm});
            skLineSegment(sketch, "E587.MirrorCS", {"start": v(-119.76, 45.19) * mm, "end": v(-115.36, 45.19) * mm});
            skPoint(sketch, "E588.MirrorP", {"position": v(-115.16, 51.29) * mm});
            skLineSegment(sketch, "E589.MirrorCS", {"start": v(-119.76, 65.19) * mm, "end": v(-115.36, 65.19) * mm});
            skArc(sketch, "E590.MirrorCS", {"start": v(-113.27, 51.29) * mm, "mid": v(-114.04, 51.14) * mm, "end": v(-114.69, 50.7) * mm});
            skArc(sketch, "E591.MirrorCS", {"start": v(-121.26, 63.69) * mm, "mid": v(-120.82, 64.75) * mm, "end": v(-119.76, 65.19) * mm});
            skPoint(sketch, "E592.MirrorP", {"position": v(-115.16, 52.35) * mm});
            skLineSegment(sketch, "E593.MirrorCS", {"start": v(-116.76, 63.39) * mm, "end": v(-116.76, 61.75) * mm});
            skLineSegment(sketch, "E594.MirrorCS", {"start": v(-114.69, 59.68) * mm, "end": v(-116.76, 61.75) * mm});
            skPoint(sketch, "E595.MirrorP", {"position": v(-115.16, 58.03) * mm});
            skLineSegment(sketch, "E596.MirrorCS", {"start": v(-119.46, 49.69) * mm, "end": v(-119.46, 52.09) * mm});
            skLineSegment(sketch, "E597.MirrorCS", {"start": v(-115.75, 51.76) * mm, "end": v(-117.82, 49.69) * mm});
            skLineSegment(sketch, "E598.MirrorCS", {"start": v(-116.76, 46.99) * mm, "end": v(-114.36, 46.99) * mm});
            skLineSegment(sketch, "E599.MirrorCS", {"start": v(-119.46, 49.69) * mm, "end": v(-117.82, 49.69) * mm});
            skLineSegment(sketch, "E600.MirrorCS", {"start": v(-121.26, 46.69) * mm, "end": v(-121.26, 49.69) * mm});
            skLineSegment(sketch, "E601.MirrorCS", {"start": v(-119.76, 65.19) * mm, "end": v(-116.76, 65.19) * mm});
            skLineSegment(sketch, "E602.MirrorCS", {"start": v(-121.26, 58.79) * mm, "end": v(-121.26, 63.69) * mm});
            skLineSegment(sketch, "E603.MirrorCS", {"start": v(-116.76, 63.39) * mm, "end": v(-114.36, 63.39) * mm});
            skLineSegment(sketch, "E604.MirrorCS", {"start": v(-114.69, 50.7) * mm, "end": v(-116.76, 48.63) * mm});
            skPoint(sketch, "E605.MirrorP", {"position": v(-114.1, 51.29) * mm});
            skLineSegment(sketch, "E606.MirrorCS", {"start": v(-119.46, 60.69) * mm, "end": v(-119.46, 58.29) * mm});
            skLineSegment(sketch, "E607.MirrorCS", {"start": v(-121.26, 63.69) * mm, "end": v(-121.26, 60.69) * mm});
            skPoint(sketch, "E608.MirrorP", {"position": v(-120.76, 51.59) * mm});
            skPoint(sketch, "E609.MirrorP", {"position": v(-121.26, 65.19) * mm});
            skPoint(sketch, "E610.MirrorP", {"position": v(-120.76, 58.79) * mm});
            skLineSegment(sketch, "E611.MirrorCS", {"start": v(-115.75, 58.61) * mm, "end": v(-117.82, 60.69) * mm});
            skLineSegment(sketch, "E612.MirrorCS", {"start": v(-119.46, 60.69) * mm, "end": v(-117.82, 60.69) * mm});
            skLineSegment(sketch, "E613.MirrorCS", {"start": v(-121.26, 46.69) * mm, "end": v(-121.26, 51.59) * mm});
            skLineSegment(sketch, "E614.MirrorCS", {"start": v(-119.76, 45.19) * mm, "end": v(-116.76, 45.19) * mm});
            skPoint(sketch, "E615.MirrorP", {"position": v(-115.16, 59.09) * mm});
            skPoint(sketch, "E616.MirrorP", {"position": v(-114.1, 59.09) * mm});
            skLineSegment(sketch, "E617.MirrorCS", {"start": v(-116.76, 46.99) * mm, "end": v(-116.76, 48.63) * mm});
            skSolve(sketch);
        }
        {
            var Q0;
            Q0=makeQuery(id+"F10.imprint","IMPRINT",FACE,{"disambiguationData":[TD([[makeQuery(id+"F10.imprint","IMPRINT",EDGE,{"derivedFrom":sQuery(id+"F10.wireOp",EDGE,"E516.bottom")}),-1.0]])]});
            extrude(context, id + "F11", {"entities" : qUnion([Q0]), "depth" : 50 * mm, "offsetDistance" : 25 * mm});
        }
        {
            var Q0;
            Q0=qCreatedBy(makeId("Top.planeOp"),FACE);
            var sketch = newSketch(context, id + "F12", { "sketchPlane" : qUnion([Q0])});
            skCircle(sketch, "E618", {"center": v(-92.98, -8.67) * mm, "radius": 2.5 * mm});
            skLineSegment(sketch, "E619.bottom", {"start": v(-84.48, -18.67) * mm, "end": v(-88.88, -18.67) * mm});
            skLineSegment(sketch, "E619.top", {"start": v(-84.48, 1.33) * mm, "end": v(-88.88, 1.33) * mm});
            skLineSegment(sketch, "E619.left", {"start": v(-82.98, -17.17) * mm, "end": v(-82.98, -12.27) * mm});
            skLineSegment(sketch, "E620.bottom", {"start": v(-90.97, -12.57) * mm, "end": v(-94.99, -12.57) * mm});
            skLineSegment(sketch, "E620.top", {"start": v(-90.97, -4.77) * mm, "end": v(-94.99, -4.77) * mm});
            skLineSegment(sketch, "E620.left", {"start": v(-89.08, -10.68) * mm, "end": v(-89.08, -6.66) * mm});
            skLineSegment(sketch, "E620.right", {"start": v(-96.88, -10.68) * mm, "end": v(-96.88, -6.66) * mm});
            skLineSegment(sketch, "E621.bottom", {"start": v(-84.48, 1.33) * mm, "end": v(-87.48, 1.33) * mm});
            skLineSegment(sketch, "E621.left", {"start": v(-82.98, -0.17) * mm, "end": v(-82.98, -3.17) * mm});
            skLineSegment(sketch, "E621.right", {"start": v(-87.48, -0.47) * mm, "end": v(-87.48, -2.1) * mm});
            skLineSegment(sketch, "E622", {"start": v(-88.5, -5.24) * mm, "end": v(-86.42, -3.17) * mm});
            skLineSegment(sketch, "E623.MirrorCS", {"start": v(-89.55, -4.18) * mm, "end": v(-87.48, -2.1) * mm});
            skLineSegment(sketch, "E624", {"start": v(-84.78, -3.17) * mm, "end": v(-84.78, -5.57) * mm});
            skLineSegment(sketch, "E625", {"start": v(-83.28, -5.07) * mm, "end": v(-82.98, -5.07) * mm});
            skLineSegment(sketch, "E626", {"start": v(-84.78, -5.57) * mm, "end": v(-83.48, -5.57) * mm});
            skLineSegment(sketch, "E627", {"start": v(-83.48, -5.27) * mm, "end": v(-83.48, -5.57) * mm});
            skPoint(sketch, "E628.visualSharp", {"position": v(-83.48, -5.07) * mm});
            skArc(sketch, "E628.filletArc", {"start": v(-83.28, -5.07) * mm, "mid": v(-83.42, -5.12) * mm, "end": v(-83.48, -5.27) * mm});
            skPoint(sketch, "E629.newPointA", {"position": v(-89.08, -5.83) * mm});
            skArc(sketch, "E629.filletArc", {"start": v(-88.5, -5.24) * mm, "mid": v(-88.93, -5.9) * mm, "end": v(-89.08, -6.66) * mm});
            skPoint(sketch, "E630.newPointA", {"position": v(-90.14, -4.77) * mm});
            skPoint(sketch, "E630.newPointB", {"position": v(-89.08, -4.77) * mm});
            skArc(sketch, "E630.filletArc", {"start": v(-90.97, -4.77) * mm, "mid": v(-90.2, -4.61) * mm, "end": v(-89.55, -4.18) * mm});
            skLineSegment(sketch, "E631.MirrorCS", {"start": v(-87.48, -0.47) * mm, "end": v(-89.88, -0.47) * mm});
            skLineSegment(sketch, "E632.MirrorCS", {"start": v(-89.88, -0.47) * mm, "end": v(-89.88, 0.83) * mm});
            skPoint(sketch, "E633.visualSharp", {"position": v(-82.98, 1.33) * mm});
            skArc(sketch, "E633.filletArc", {"start": v(-82.98, -0.17) * mm, "mid": v(-83.42, 0.9) * mm, "end": v(-84.48, 1.33) * mm});
            skLineSegment(sketch, "E634.trimOffspring", {"start": v(-84.78, -3.17) * mm, "end": v(-86.42, -3.17) * mm});
            skLineSegment(sketch, "E635.MirrorCS", {"start": v(-83.28, -12.27) * mm, "end": v(-82.98, -12.27) * mm});
            skArc(sketch, "E636.MirrorCS", {"start": v(-83.28, -12.27) * mm, "mid": v(-83.42, -12.2) * mm, "end": v(-83.48, -12.07) * mm});
            skLineSegment(sketch, "E637.MirrorCS", {"start": v(-83.48, -12.07) * mm, "end": v(-83.48, -11.77) * mm});
            skArc(sketch, "E638.MirrorCS", {"start": v(-88.5, -12.1) * mm, "mid": v(-88.93, -11.44) * mm, "end": v(-89.08, -10.68) * mm});
            skLineSegment(sketch, "E639.MirrorCS", {"start": v(-84.78, -14.17) * mm, "end": v(-86.42, -14.17) * mm});
            skLineSegment(sketch, "E640.MirrorCS", {"start": v(-84.78, -11.77) * mm, "end": v(-83.48, -11.77) * mm});
            skLineSegment(sketch, "E641.MirrorCS", {"start": v(-84.48, -18.67) * mm, "end": v(-87.48, -18.67) * mm});
            skPoint(sketch, "E642.MirrorP", {"position": v(-83.48, -12.27) * mm});
            skLineSegment(sketch, "E643.MirrorCS", {"start": v(-89.88, -16.87) * mm, "end": v(-89.88, -18.17) * mm});
            skLineSegment(sketch, "E644.MirrorCS", {"start": v(-87.48, -16.87) * mm, "end": v(-89.88, -16.87) * mm});
            skLineSegment(sketch, "E645.MirrorCS", {"start": v(-84.78, -14.17) * mm, "end": v(-84.78, -11.77) * mm});
            skLineSegment(sketch, "E646.MirrorCS", {"start": v(-82.98, -17.17) * mm, "end": v(-82.98, -14.17) * mm});
            skLineSegment(sketch, "E647.MirrorCS", {"start": v(-88.5, -12.1) * mm, "end": v(-86.42, -14.17) * mm});
            skPoint(sketch, "E648.MirrorP", {"position": v(-89.08, -11.5) * mm});
            skPoint(sketch, "E649.MirrorP", {"position": v(-82.98, -18.67) * mm});
            skPoint(sketch, "E650.MirrorP", {"position": v(-89.08, -12.57) * mm});
            skLineSegment(sketch, "E651.MirrorCS", {"start": v(-89.55, -13.15) * mm, "end": v(-87.48, -15.23) * mm});
            skPoint(sketch, "E652.MirrorP", {"position": v(-90.14, -12.57) * mm});
            skArc(sketch, "E653.MirrorCS", {"start": v(-82.98, -17.17) * mm, "mid": v(-83.42, -18.23) * mm, "end": v(-84.48, -18.67) * mm});
            skLineSegment(sketch, "E654.MirrorCS", {"start": v(-87.48, -16.87) * mm, "end": v(-87.48, -15.23) * mm});
            skArc(sketch, "E655.MirrorCS", {"start": v(-90.97, -12.57) * mm, "mid": v(-90.2, -12.72) * mm, "end": v(-89.55, -13.15) * mm});
            skLineSegment(sketch, "E656.trimOffspring", {"start": v(-82.98, -5.07) * mm, "end": v(-82.98, -0.17) * mm});
            skLineSegment(sketch, "E657.MirrorCS", {"start": v(-89.38, 1.03) * mm, "end": v(-89.38, 1.33) * mm});
            skArc(sketch, "E658.MirrorCS", {"start": v(-89.38, 1.03) * mm, "mid": v(-89.44, 0.9) * mm, "end": v(-89.58, 0.83) * mm});
            skLineSegment(sketch, "E659.MirrorCS", {"start": v(-89.58, 0.83) * mm, "end": v(-89.88, 0.83) * mm});
            skLineSegment(sketch, "E660", {"start": v(-88.88, 1.33) * mm, "end": v(-89.38, 1.33) * mm});
            skLineSegment(sketch, "E661.MirrorCS", {"start": v(-89.38, -18.37) * mm, "end": v(-89.38, -18.67) * mm});
            skLineSegment(sketch, "E662.MirrorCS", {"start": v(-89.58, -18.17) * mm, "end": v(-89.88, -18.17) * mm});
            skLineSegment(sketch, "E663.MirrorCS", {"start": v(-88.88, -18.67) * mm, "end": v(-89.38, -18.67) * mm});
            skArc(sketch, "E664.MirrorCS", {"start": v(-89.38, -18.37) * mm, "mid": v(-89.44, -18.22) * mm, "end": v(-89.58, -18.17) * mm});
            skArc(sketch, "E665.MirrorCS", {"start": v(-102.68, -12.27) * mm, "mid": v(-102.54, -12.2) * mm, "end": v(-102.48, -12.07) * mm});
            skLineSegment(sketch, "E666.MirrorCS", {"start": v(-102.68, -5.07) * mm, "end": v(-102.98, -5.07) * mm});
            skLineSegment(sketch, "E667.MirrorCS", {"start": v(-102.48, -12.07) * mm, "end": v(-102.48, -11.77) * mm});
            skArc(sketch, "E668.MirrorCS", {"start": v(-102.68, -5.07) * mm, "mid": v(-102.54, -5.12) * mm, "end": v(-102.48, -5.27) * mm});
            skLineSegment(sketch, "E669.MirrorCS", {"start": v(-102.48, -5.27) * mm, "end": v(-102.48, -5.57) * mm});
            skLineSegment(sketch, "E670.MirrorCS", {"start": v(-102.68, -12.27) * mm, "end": v(-102.98, -12.27) * mm});
            skLineSegment(sketch, "E671.MirrorCS", {"start": v(-97.08, 1.33) * mm, "end": v(-96.58, 1.33) * mm});
            skArc(sketch, "E672.MirrorCS", {"start": v(-102.98, -17.17) * mm, "mid": v(-102.54, -18.23) * mm, "end": v(-101.48, -18.67) * mm});
            skLineSegment(sketch, "E673.MirrorCS", {"start": v(-96.58, 1.03) * mm, "end": v(-96.58, 1.33) * mm});
            skArc(sketch, "E674.MirrorCS", {"start": v(-97.46, -5.24) * mm, "mid": v(-97.03, -5.9) * mm, "end": v(-96.88, -6.66) * mm});
            skLineSegment(sketch, "E675.MirrorCS", {"start": v(-96.38, -18.17) * mm, "end": v(-96.08, -18.17) * mm});
            skLineSegment(sketch, "E676.MirrorCS", {"start": v(-96.08, -0.47) * mm, "end": v(-96.08, 0.83) * mm});
            skLineSegment(sketch, "E677.MirrorCS", {"start": v(-94.99, -4.77) * mm, "end": v(-90.97, -4.77) * mm});
            skLineSegment(sketch, "E678.MirrorCS", {"start": v(-101.18, -11.77) * mm, "end": v(-102.48, -11.77) * mm});
            skLineSegment(sketch, "E679.MirrorCS", {"start": v(-101.18, -5.57) * mm, "end": v(-102.48, -5.57) * mm});
            skLineSegment(sketch, "E680.MirrorCS", {"start": v(-96.38, 0.83) * mm, "end": v(-96.08, 0.83) * mm});
            skArc(sketch, "E681.MirrorCS", {"start": v(-97.46, -12.1) * mm, "mid": v(-97.03, -11.44) * mm, "end": v(-96.88, -10.68) * mm});
            skArc(sketch, "E682.MirrorCS", {"start": v(-96.58, -18.37) * mm, "mid": v(-96.52, -18.22) * mm, "end": v(-96.38, -18.17) * mm});
            skArc(sketch, "E683.MirrorCS", {"start": v(-96.58, 1.03) * mm, "mid": v(-96.52, 0.9) * mm, "end": v(-96.38, 0.83) * mm});
            skLineSegment(sketch, "E684.MirrorCS", {"start": v(-96.58, -18.37) * mm, "end": v(-96.58, -18.67) * mm});
            skLineSegment(sketch, "E685.MirrorCS", {"start": v(-94.99, -12.57) * mm, "end": v(-90.97, -12.57) * mm});
            skLineSegment(sketch, "E686.MirrorCS", {"start": v(-97.08, -18.67) * mm, "end": v(-96.58, -18.67) * mm});
            skLineSegment(sketch, "E687.MirrorCS", {"start": v(-96.08, -16.87) * mm, "end": v(-96.08, -18.17) * mm});
            skArc(sketch, "E688.MirrorCS", {"start": v(-94.99, -4.77) * mm, "mid": v(-95.75, -4.61) * mm, "end": v(-96.4, -4.18) * mm});
            skPoint(sketch, "E689.MirrorP", {"position": v(-102.98, -18.67) * mm});
            skLineSegment(sketch, "E690.MirrorCS", {"start": v(-101.48, -18.67) * mm, "end": v(-97.08, -18.67) * mm});
            skPoint(sketch, "E691.MirrorP", {"position": v(-96.88, -12.57) * mm});
            skLineSegment(sketch, "E692.MirrorCS", {"start": v(-101.48, 1.33) * mm, "end": v(-97.08, 1.33) * mm});
            skArc(sketch, "E693.MirrorCS", {"start": v(-94.99, -12.57) * mm, "mid": v(-95.75, -12.72) * mm, "end": v(-96.4, -13.15) * mm});
            skArc(sketch, "E694.MirrorCS", {"start": v(-102.98, -0.17) * mm, "mid": v(-102.54, 0.9) * mm, "end": v(-101.48, 1.33) * mm});
            skPoint(sketch, "E695.MirrorP", {"position": v(-96.88, -11.5) * mm});
            skLineSegment(sketch, "E696.MirrorCS", {"start": v(-98.48, -0.47) * mm, "end": v(-98.48, -2.1) * mm});
            skLineSegment(sketch, "E697.MirrorCS", {"start": v(-96.4, -4.18) * mm, "end": v(-98.48, -2.1) * mm});
            skPoint(sketch, "E698.MirrorP", {"position": v(-96.88, -5.83) * mm});
            skLineSegment(sketch, "E699.MirrorCS", {"start": v(-101.18, -14.17) * mm, "end": v(-101.18, -11.77) * mm});
            skLineSegment(sketch, "E700.MirrorCS", {"start": v(-97.46, -12.1) * mm, "end": v(-99.54, -14.17) * mm});
            skLineSegment(sketch, "E701.MirrorCS", {"start": v(-98.48, -16.87) * mm, "end": v(-96.08, -16.87) * mm});
            skLineSegment(sketch, "E702.MirrorCS", {"start": v(-101.18, -14.17) * mm, "end": v(-99.54, -14.17) * mm});
            skLineSegment(sketch, "E703.MirrorCS", {"start": v(-102.98, -17.17) * mm, "end": v(-102.98, -14.17) * mm});
            skLineSegment(sketch, "E704.MirrorCS", {"start": v(-101.48, 1.33) * mm, "end": v(-98.48, 1.33) * mm});
            skLineSegment(sketch, "E705.MirrorCS", {"start": v(-102.98, -5.07) * mm, "end": v(-102.98, -0.17) * mm});
            skLineSegment(sketch, "E706.MirrorCS", {"start": v(-98.48, -0.47) * mm, "end": v(-96.08, -0.47) * mm});
            skLineSegment(sketch, "E707.MirrorCS", {"start": v(-96.4, -13.15) * mm, "end": v(-98.48, -15.23) * mm});
            skPoint(sketch, "E708.MirrorP", {"position": v(-95.82, -12.57) * mm});
            skLineSegment(sketch, "E709.MirrorCS", {"start": v(-101.18, -3.17) * mm, "end": v(-101.18, -5.57) * mm});
            skLineSegment(sketch, "E710.MirrorCS", {"start": v(-102.98, -0.17) * mm, "end": v(-102.98, -3.17) * mm});
            skPoint(sketch, "E711.MirrorP", {"position": v(-102.48, -12.27) * mm});
            skPoint(sketch, "E712.MirrorP", {"position": v(-102.98, 1.33) * mm});
            skPoint(sketch, "E713.MirrorP", {"position": v(-102.48, -5.07) * mm});
            skLineSegment(sketch, "E714.MirrorCS", {"start": v(-97.46, -5.24) * mm, "end": v(-99.54, -3.17) * mm});
            skLineSegment(sketch, "E715.MirrorCS", {"start": v(-101.18, -3.17) * mm, "end": v(-99.54, -3.17) * mm});
            skLineSegment(sketch, "E716.MirrorCS", {"start": v(-102.98, -17.17) * mm, "end": v(-102.98, -12.27) * mm});
            skLineSegment(sketch, "E717.MirrorCS", {"start": v(-101.48, -18.67) * mm, "end": v(-98.48, -18.67) * mm});
            skPoint(sketch, "E718.MirrorP", {"position": v(-96.88, -4.77) * mm});
            skPoint(sketch, "E719.MirrorP", {"position": v(-95.82, -4.77) * mm});
            skLineSegment(sketch, "E720.MirrorCS", {"start": v(-98.48, -16.87) * mm, "end": v(-98.48, -15.23) * mm});
            skSolve(sketch);
        }
        {
            var Q0;
            Q0=makeQuery(id+"F12.imprint","IMPRINT",FACE,{"disambiguationData":[TD([[makeQuery(id+"F12.imprint","IMPRINT",EDGE,{"derivedFrom":sQuery(id+"F12.wireOp",EDGE,"E619.bottom")}),-1.0]])]});
            extrude(context, id + "F13", {"entities" : qUnion([Q0]), "depth" : 55 * mm, "offsetDistance" : 25 * mm});
        }
        {
            var Q0;
            Q0=qCreatedBy(makeId("Top.planeOp"),FACE);
            var sketch = newSketch(context, id + "F14", { "sketchPlane" : qUnion([Q0])});
            skCircle(sketch, "E721", {"center": v(-102, -38) * mm, "radius": 2.5 * mm});
            skLineSegment(sketch, "E722.bottom", {"start": v(-93.5, -48) * mm, "end": v(-97.9, -48) * mm});
            skLineSegment(sketch, "E722.top", {"start": v(-93.5, -28) * mm, "end": v(-97.9, -28) * mm});
            skLineSegment(sketch, "E722.left", {"start": v(-92, -46.5) * mm, "end": v(-92, -41.6) * mm});
            skLineSegment(sketch, "E723.bottom", {"start": v(-100, -41.9) * mm, "end": v(-104.01, -41.9) * mm});
            skLineSegment(sketch, "E723.top", {"start": v(-100, -34.1) * mm, "end": v(-104.01, -34.1) * mm});
            skLineSegment(sketch, "E723.left", {"start": v(-98.1, -40) * mm, "end": v(-98.1, -35.98) * mm});
            skLineSegment(sketch, "E723.right", {"start": v(-105.9, -40) * mm, "end": v(-105.9, -35.98) * mm});
            skLineSegment(sketch, "E724.bottom", {"start": v(-93.5, -28) * mm, "end": v(-96.5, -28) * mm});
            skLineSegment(sketch, "E724.left", {"start": v(-92, -29.5) * mm, "end": v(-92, -32.5) * mm});
            skLineSegment(sketch, "E724.right", {"start": v(-96.5, -29.8) * mm, "end": v(-96.5, -31.43) * mm});
            skLineSegment(sketch, "E725", {"start": v(-97.52, -34.57) * mm, "end": v(-95.44, -32.5) * mm});
            skLineSegment(sketch, "E726.MirrorCS", {"start": v(-98.58, -33.5) * mm, "end": v(-96.5, -31.43) * mm});
            skLineSegment(sketch, "E727", {"start": v(-93.8, -32.5) * mm, "end": v(-93.8, -34.9) * mm});
            skLineSegment(sketch, "E728", {"start": v(-92.3, -34.4) * mm, "end": v(-92, -34.4) * mm});
            skLineSegment(sketch, "E729", {"start": v(-93.8, -34.9) * mm, "end": v(-92.5, -34.9) * mm});
            skLineSegment(sketch, "E730", {"start": v(-92.5, -34.6) * mm, "end": v(-92.5, -34.9) * mm});
            skPoint(sketch, "E731.visualSharp", {"position": v(-92.5, -34.4) * mm});
            skArc(sketch, "E731.filletArc", {"start": v(-92.3, -34.4) * mm, "mid": v(-92.44, -34.45) * mm, "end": v(-92.5, -34.6) * mm});
            skPoint(sketch, "E732.newPointA", {"position": v(-98.1, -35.16) * mm});
            skArc(sketch, "E732.filletArc", {"start": v(-97.52, -34.57) * mm, "mid": v(-97.95, -35.22) * mm, "end": v(-98.1, -35.98) * mm});
            skPoint(sketch, "E733.newPointA", {"position": v(-99.16, -34.1) * mm});
            skPoint(sketch, "E733.newPointB", {"position": v(-98.1, -34.1) * mm});
            skArc(sketch, "E733.filletArc", {"start": v(-100, -34.1) * mm, "mid": v(-99.23, -33.94) * mm, "end": v(-98.58, -33.5) * mm});
            skLineSegment(sketch, "E734.MirrorCS", {"start": v(-96.5, -29.8) * mm, "end": v(-98.9, -29.8) * mm});
            skLineSegment(sketch, "E735.MirrorCS", {"start": v(-98.9, -29.8) * mm, "end": v(-98.9, -28.5) * mm});
            skPoint(sketch, "E736.visualSharp", {"position": v(-92, -28) * mm});
            skArc(sketch, "E736.filletArc", {"start": v(-92, -29.5) * mm, "mid": v(-92.44, -28.43) * mm, "end": v(-93.5, -28) * mm});
            skLineSegment(sketch, "E737.trimOffspring", {"start": v(-93.8, -32.5) * mm, "end": v(-95.44, -32.5) * mm});
            skLineSegment(sketch, "E738.MirrorCS", {"start": v(-92.3, -41.6) * mm, "end": v(-92, -41.6) * mm});
            skArc(sketch, "E739.MirrorCS", {"start": v(-92.3, -41.6) * mm, "mid": v(-92.44, -41.54) * mm, "end": v(-92.5, -41.4) * mm});
            skLineSegment(sketch, "E740.MirrorCS", {"start": v(-92.5, -41.4) * mm, "end": v(-92.5, -41.1) * mm});
            skArc(sketch, "E741.MirrorCS", {"start": v(-97.52, -41.42) * mm, "mid": v(-97.95, -40.77) * mm, "end": v(-98.1, -40) * mm});
            skLineSegment(sketch, "E742.MirrorCS", {"start": v(-93.8, -43.5) * mm, "end": v(-95.44, -43.5) * mm});
            skLineSegment(sketch, "E743.MirrorCS", {"start": v(-93.8, -41.1) * mm, "end": v(-92.5, -41.1) * mm});
            skLineSegment(sketch, "E744.MirrorCS", {"start": v(-93.5, -48) * mm, "end": v(-96.5, -48) * mm});
            skPoint(sketch, "E745.MirrorP", {"position": v(-92.5, -41.6) * mm});
            skLineSegment(sketch, "E746.MirrorCS", {"start": v(-98.9, -46.2) * mm, "end": v(-98.9, -47.5) * mm});
            skLineSegment(sketch, "E747.MirrorCS", {"start": v(-96.5, -46.2) * mm, "end": v(-98.9, -46.2) * mm});
            skLineSegment(sketch, "E748.MirrorCS", {"start": v(-93.8, -43.5) * mm, "end": v(-93.8, -41.1) * mm});
            skLineSegment(sketch, "E749.MirrorCS", {"start": v(-92, -46.5) * mm, "end": v(-92, -43.5) * mm});
            skLineSegment(sketch, "E750.MirrorCS", {"start": v(-97.52, -41.42) * mm, "end": v(-95.44, -43.5) * mm});
            skPoint(sketch, "E751.MirrorP", {"position": v(-98.1, -40.83) * mm});
            skPoint(sketch, "E752.MirrorP", {"position": v(-92, -48) * mm});
            skPoint(sketch, "E753.MirrorP", {"position": v(-98.1, -41.9) * mm});
            skLineSegment(sketch, "E754.MirrorCS", {"start": v(-98.58, -42.48) * mm, "end": v(-96.5, -44.56) * mm});
            skPoint(sketch, "E755.MirrorP", {"position": v(-99.16, -41.9) * mm});
            skArc(sketch, "E756.MirrorCS", {"start": v(-92, -46.5) * mm, "mid": v(-92.44, -47.56) * mm, "end": v(-93.5, -48) * mm});
            skLineSegment(sketch, "E757.MirrorCS", {"start": v(-96.5, -46.2) * mm, "end": v(-96.5, -44.56) * mm});
            skArc(sketch, "E758.MirrorCS", {"start": v(-100, -41.9) * mm, "mid": v(-99.23, -42.05) * mm, "end": v(-98.58, -42.48) * mm});
            skLineSegment(sketch, "E759.trimOffspring", {"start": v(-92, -34.4) * mm, "end": v(-92, -29.5) * mm});
            skLineSegment(sketch, "E760.MirrorCS", {"start": v(-98.4, -28.3) * mm, "end": v(-98.4, -28) * mm});
            skArc(sketch, "E761.MirrorCS", {"start": v(-98.4, -28.3) * mm, "mid": v(-98.46, -28.44) * mm, "end": v(-98.6, -28.5) * mm});
            skLineSegment(sketch, "E762.MirrorCS", {"start": v(-98.6, -28.5) * mm, "end": v(-98.9, -28.5) * mm});
            skLineSegment(sketch, "E763", {"start": v(-97.9, -28) * mm, "end": v(-98.4, -28) * mm});
            skLineSegment(sketch, "E764.MirrorCS", {"start": v(-98.4, -47.7) * mm, "end": v(-98.4, -48) * mm});
            skLineSegment(sketch, "E765.MirrorCS", {"start": v(-98.6, -47.5) * mm, "end": v(-98.9, -47.5) * mm});
            skLineSegment(sketch, "E766.MirrorCS", {"start": v(-97.9, -48) * mm, "end": v(-98.4, -48) * mm});
            skArc(sketch, "E767.MirrorCS", {"start": v(-98.4, -47.7) * mm, "mid": v(-98.46, -47.55) * mm, "end": v(-98.6, -47.5) * mm});
            skArc(sketch, "E768.MirrorCS", {"start": v(-111.7, -41.6) * mm, "mid": v(-111.56, -41.54) * mm, "end": v(-111.5, -41.4) * mm});
            skLineSegment(sketch, "E769.MirrorCS", {"start": v(-111.7, -34.4) * mm, "end": v(-112, -34.4) * mm});
            skLineSegment(sketch, "E770.MirrorCS", {"start": v(-111.5, -41.4) * mm, "end": v(-111.5, -41.1) * mm});
            skArc(sketch, "E771.MirrorCS", {"start": v(-111.7, -34.4) * mm, "mid": v(-111.56, -34.45) * mm, "end": v(-111.5, -34.6) * mm});
            skLineSegment(sketch, "E772.MirrorCS", {"start": v(-111.5, -34.6) * mm, "end": v(-111.5, -34.9) * mm});
            skLineSegment(sketch, "E773.MirrorCS", {"start": v(-111.7, -41.6) * mm, "end": v(-112, -41.6) * mm});
            skLineSegment(sketch, "E774.MirrorCS", {"start": v(-106.1, -28) * mm, "end": v(-105.6, -28) * mm});
            skArc(sketch, "E775.MirrorCS", {"start": v(-112, -46.5) * mm, "mid": v(-111.56, -47.56) * mm, "end": v(-110.5, -48) * mm});
            skLineSegment(sketch, "E776.MirrorCS", {"start": v(-105.6, -28.3) * mm, "end": v(-105.6, -28) * mm});
            skArc(sketch, "E777.MirrorCS", {"start": v(-106.49, -34.57) * mm, "mid": v(-106.05, -35.22) * mm, "end": v(-105.9, -35.98) * mm});
            skLineSegment(sketch, "E778.MirrorCS", {"start": v(-105.4, -47.5) * mm, "end": v(-105.1, -47.5) * mm});
            skLineSegment(sketch, "E779.MirrorCS", {"start": v(-105.1, -29.8) * mm, "end": v(-105.1, -28.5) * mm});
            skLineSegment(sketch, "E780.MirrorCS", {"start": v(-104.01, -34.1) * mm, "end": v(-100, -34.1) * mm});
            skLineSegment(sketch, "E781.MirrorCS", {"start": v(-110.2, -41.1) * mm, "end": v(-111.5, -41.1) * mm});
            skLineSegment(sketch, "E782.MirrorCS", {"start": v(-110.2, -34.9) * mm, "end": v(-111.5, -34.9) * mm});
            skLineSegment(sketch, "E783.MirrorCS", {"start": v(-105.4, -28.5) * mm, "end": v(-105.1, -28.5) * mm});
            skArc(sketch, "E784.MirrorCS", {"start": v(-106.49, -41.42) * mm, "mid": v(-106.05, -40.77) * mm, "end": v(-105.9, -40) * mm});
            skArc(sketch, "E785.MirrorCS", {"start": v(-105.6, -47.7) * mm, "mid": v(-105.54, -47.55) * mm, "end": v(-105.4, -47.5) * mm});
            skArc(sketch, "E786.MirrorCS", {"start": v(-105.6, -28.3) * mm, "mid": v(-105.54, -28.44) * mm, "end": v(-105.4, -28.5) * mm});
            skLineSegment(sketch, "E787.MirrorCS", {"start": v(-105.6, -47.7) * mm, "end": v(-105.6, -48) * mm});
            skLineSegment(sketch, "E788.MirrorCS", {"start": v(-104.01, -41.9) * mm, "end": v(-100, -41.9) * mm});
            skLineSegment(sketch, "E789.MirrorCS", {"start": v(-106.1, -48) * mm, "end": v(-105.6, -48) * mm});
            skLineSegment(sketch, "E790.MirrorCS", {"start": v(-105.1, -46.2) * mm, "end": v(-105.1, -47.5) * mm});
            skArc(sketch, "E791.MirrorCS", {"start": v(-104.01, -34.1) * mm, "mid": v(-104.78, -33.94) * mm, "end": v(-105.43, -33.5) * mm});
            skPoint(sketch, "E792.MirrorP", {"position": v(-112, -48) * mm});
            skLineSegment(sketch, "E793.MirrorCS", {"start": v(-110.5, -48) * mm, "end": v(-106.1, -48) * mm});
            skPoint(sketch, "E794.MirrorP", {"position": v(-105.9, -41.9) * mm});
            skLineSegment(sketch, "E795.MirrorCS", {"start": v(-110.5, -28) * mm, "end": v(-106.1, -28) * mm});
            skArc(sketch, "E796.MirrorCS", {"start": v(-104.01, -41.9) * mm, "mid": v(-104.78, -42.05) * mm, "end": v(-105.43, -42.48) * mm});
            skArc(sketch, "E797.MirrorCS", {"start": v(-112, -29.5) * mm, "mid": v(-111.56, -28.43) * mm, "end": v(-110.5, -28) * mm});
            skPoint(sketch, "E798.MirrorP", {"position": v(-105.9, -40.83) * mm});
            skLineSegment(sketch, "E799.MirrorCS", {"start": v(-107.5, -29.8) * mm, "end": v(-107.5, -31.43) * mm});
            skLineSegment(sketch, "E800.MirrorCS", {"start": v(-105.43, -33.5) * mm, "end": v(-107.5, -31.43) * mm});
            skPoint(sketch, "E801.MirrorP", {"position": v(-105.9, -35.16) * mm});
            skLineSegment(sketch, "E802.MirrorCS", {"start": v(-110.2, -43.5) * mm, "end": v(-110.2, -41.1) * mm});
            skLineSegment(sketch, "E803.MirrorCS", {"start": v(-106.49, -41.42) * mm, "end": v(-108.56, -43.5) * mm});
            skLineSegment(sketch, "E804.MirrorCS", {"start": v(-107.5, -46.2) * mm, "end": v(-105.1, -46.2) * mm});
            skLineSegment(sketch, "E805.MirrorCS", {"start": v(-110.2, -43.5) * mm, "end": v(-108.56, -43.5) * mm});
            skLineSegment(sketch, "E806.MirrorCS", {"start": v(-112, -46.5) * mm, "end": v(-112, -43.5) * mm});
            skLineSegment(sketch, "E807.MirrorCS", {"start": v(-110.5, -28) * mm, "end": v(-107.5, -28) * mm});
            skLineSegment(sketch, "E808.MirrorCS", {"start": v(-112, -34.4) * mm, "end": v(-112, -29.5) * mm});
            skLineSegment(sketch, "E809.MirrorCS", {"start": v(-107.5, -29.8) * mm, "end": v(-105.1, -29.8) * mm});
            skLineSegment(sketch, "E810.MirrorCS", {"start": v(-105.43, -42.48) * mm, "end": v(-107.5, -44.56) * mm});
            skPoint(sketch, "E811.MirrorP", {"position": v(-104.84, -41.9) * mm});
            skLineSegment(sketch, "E812.MirrorCS", {"start": v(-110.2, -32.5) * mm, "end": v(-110.2, -34.9) * mm});
            skLineSegment(sketch, "E813.MirrorCS", {"start": v(-112, -29.5) * mm, "end": v(-112, -32.5) * mm});
            skPoint(sketch, "E814.MirrorP", {"position": v(-111.5, -41.6) * mm});
            skPoint(sketch, "E815.MirrorP", {"position": v(-112, -28) * mm});
            skPoint(sketch, "E816.MirrorP", {"position": v(-111.5, -34.4) * mm});
            skLineSegment(sketch, "E817.MirrorCS", {"start": v(-106.49, -34.57) * mm, "end": v(-108.56, -32.5) * mm});
            skLineSegment(sketch, "E818.MirrorCS", {"start": v(-110.2, -32.5) * mm, "end": v(-108.56, -32.5) * mm});
            skLineSegment(sketch, "E819.MirrorCS", {"start": v(-112, -46.5) * mm, "end": v(-112, -41.6) * mm});
            skLineSegment(sketch, "E820.MirrorCS", {"start": v(-110.5, -48) * mm, "end": v(-107.5, -48) * mm});
            skPoint(sketch, "E821.MirrorP", {"position": v(-105.9, -34.1) * mm});
            skPoint(sketch, "E822.MirrorP", {"position": v(-104.84, -34.1) * mm});
            skLineSegment(sketch, "E823.MirrorCS", {"start": v(-107.5, -46.2) * mm, "end": v(-107.5, -44.56) * mm});
            skSolve(sketch);
        }
        {
            var Q0;
            Q0=makeQuery(id+"F14.imprint","IMPRINT",FACE,{"disambiguationData":[TD([[makeQuery(id+"F14.imprint","IMPRINT",EDGE,{"derivedFrom":sQuery(id+"F14.wireOp",EDGE,"E722.bottom")}),-1.0]])]});
            extrude(context, id + "F15", {"entities" : qUnion([Q0]), "depth" : 75 * mm, "offsetDistance" : 25 * mm});
        }
    });
